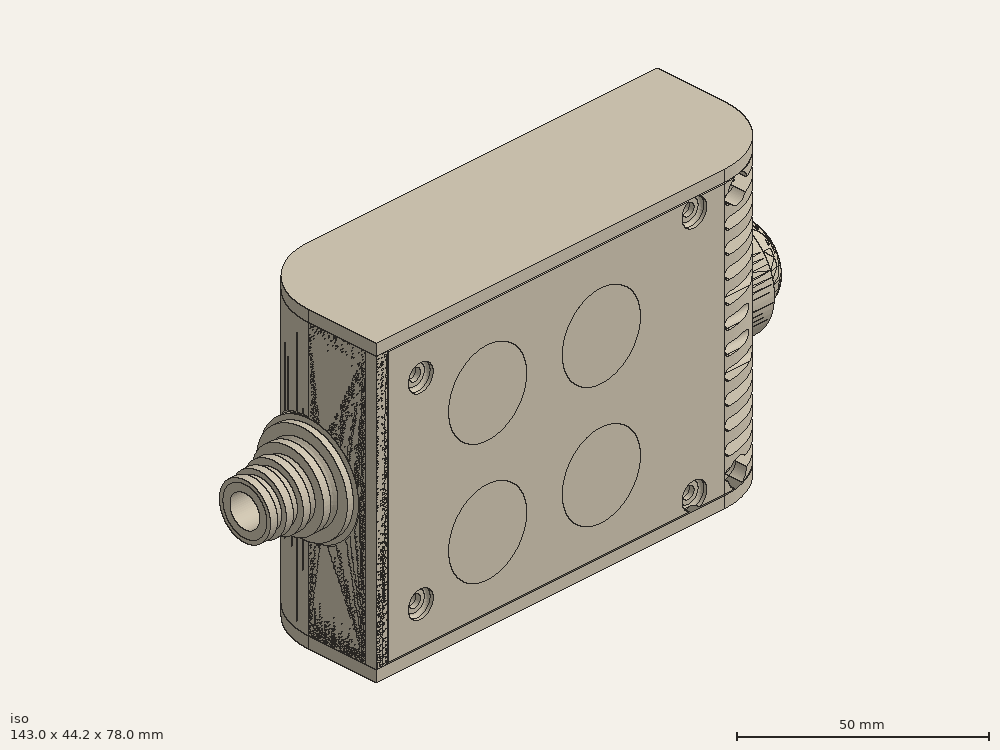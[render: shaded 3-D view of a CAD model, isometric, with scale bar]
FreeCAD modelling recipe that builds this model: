
FCSTD DOCUMENT  (FreeCAD 0.19R0.19.2)
Label: enclosure_123
License: All rights reserved
LicenseURL: http://en.wikipedia.org/wiki/All_rights_reserved
objects: Part::Feature×72, Part::Revolution×72, Part::MultiFuse×61, Sketcher::SketchObject×34, Part::Fillet×26, Part::Cut×24, Part::Extrusion×23, Part::Cylinder×22, Part::Box×12, App::MeasureDistance×4
note: 346 computed .brp shape members not serialized (recipe doc carries the construction recipe); baked Part::Feature solids carry a one-line shape summary decoded from their .brp

FEATURE [Sketcher::SketchObject] Sketch  label="topSketch"
  FullyConstrained = true
  sketch-geometry (13):
    g0: LineSegment StartX=117 StartY=19 StartZ=0 EndX=117 EndY=38 EndZ=0
    g1: ArcOfCircle CenterX=98 CenterY=19 CenterZ=0 NormalX=0 NormalY=0 NormalZ=1 AngleXU=0 Radius=19 StartAngle=5.7297 EndAngle=6.28319
    g2: LineSegment StartX=0 StartY=3 StartZ=0 EndX=0 EndY=19 EndZ=0
    g3: LineSegment StartX=19 StartY=38 StartZ=0 EndX=117 EndY=38 EndZ=0
    g4: ArcOfCircle CenterX=19 CenterY=19 CenterZ=0 NormalX=0 NormalY=0 NormalZ=1 AngleXU=0 Radius=19 StartAngle=1.5708 EndAngle=3.14159
    g5: ArcOfCircle CenterX=19 CenterY=19 CenterZ=0 NormalX=0 NormalY=0 NormalZ=1 AngleXU=0 Radius=16 StartAngle=1.5708 EndAngle=3.14159
    g6: ArcOfCircle CenterX=98 CenterY=19 CenterZ=0 NormalX=0 NormalY=0 NormalZ=1 AngleXU=0 Radius=16 StartAngle=5.60905 EndAngle=6.28319
    g7: LineSegment StartX=114 StartY=19 StartZ=0 EndX=114 EndY=35 EndZ=0
    g8: LineSegment StartX=110.5 StartY=9.01251 StartZ=0 EndX=114.163 EndY=9.01251 EndZ=0
    g9: LineSegment StartX=114 StartY=35 StartZ=0 EndX=19 EndY=35 EndZ=0
    g10: LineSegment StartX=0 StartY=3 StartZ=0 EndX=0 EndY=0 EndZ=0
    g11: LineSegment StartX=3 StartY=0 StartZ=0 EndX=0 EndY=0 EndZ=0
    g12: LineSegment StartX=3 StartY=19 StartZ=0 EndX=3 EndY=0 EndZ=0
  constraints (33):
    c: Vertical(g0)
    c: Distance(g0) = 19
    c: Block(g0)
    c: Coincident(g1,g0)
    c: Block(g1)
    c: Vertical(g2)
    c: Block(g2)
    c: Coincident(g3,g0)
    c: Horizontal(g3)
    c: Distance(g3) = 98
    c: Coincident(g4,g3)
    c: Coincident(g4,g2)
    c: Block(g4)
    c: Coincident(g5,g4)
    c: Coincident(g6,g1)
    c: Block(g6)
    c: Block(g5)
    c: Coincident(g7,g6)
    c: Vertical(g7)
    c: Coincident(g8,g6)
    c: Coincident(g8,g1)
    c: Coincident(g9,g7)
    c: Coincident(g9,g5)
    c: Horizontal(g9)
    c: Tangent(g9,g5)
    c: Coincident(g10,g2)
    c: Distance(g10) = 3
    c: Vertical(g10)
    c: Coincident(g11,g10)
    c: Horizontal(g11)
    c: Coincident(g12,g5)
    c: Coincident(g12,g11)
    c: Vertical(g12)
FEATURE [Sketcher::SketchObject] Sketch001  label="bottomSketch"
  FullyConstrained = true
  sketch-geometry (32):
    g0: LineSegment StartX=3.3 StartY=-6.03275e-07 StartZ=0 EndX=98 EndY=-6.03275e-07 EndZ=0
    g1: ArcOfCircle CenterX=98 CenterY=19 CenterZ=0 NormalX=0 NormalY=0 NormalZ=1 AngleXU=0 Radius=19 StartAngle=4.71239 EndAngle=5.71103
    g2: LineSegment StartX=6.3 StartY=8 StartZ=0 EndX=3.3 EndY=8 EndZ=0
    g3: LineSegment StartX=3.3 StartY=8 StartZ=0 EndX=3.3 EndY=-6.03275e-07 EndZ=0
    g4: ArcOfCircle CenterX=8.3 CenterY=5 CenterZ=0 NormalX=0 NormalY=0 NormalZ=1 AngleXU=0 Radius=2 StartAngle=3.14159 EndAngle=4.71239
    g5: LineSegment StartX=6.3 StartY=8 StartZ=0 EndX=6.3 EndY=5 EndZ=0
    g6: ArcOfCircle CenterX=98 CenterY=19 CenterZ=0 NormalX=0 NormalY=0 NormalZ=1 AngleXU=0 Radius=12.7 StartAngle=4.71239 EndAngle=6.28319
    g7: LineSegment StartX=94.7 StartY=3 StartZ=0 EndX=8.3 EndY=3 EndZ=0
    g8-g12: Circle x5 (B-spline internal-alignment scaffolding for g13; pole/knot coordinates omitted)
    g13: BSplineCurve PolesCount=5 KnotsCount=3 Degree=3 IsPeriodic=0
    g14: GeomPoint X=98 Y=6.3 Z=0
    g15: GeomPoint X=96.3938 Y=4.71946 Z=0
    g16: GeomPoint X=94.7 Y=3 Z=0
    g17-g23: Circle x7 (B-spline internal-alignment scaffolding for g24; pole/knot coordinates omitted)
    g24: BSplineCurve PolesCount=7 KnotsCount=5 Degree=3 IsPeriodic=0
    g25-g29: GeomPoint x5 (B-spline internal-alignment scaffolding for g24; pole/knot coordinates omitted)
    g30: ArcOfCircle CenterX=98 CenterY=19 CenterZ=0 NormalX=0 NormalY=0 NormalZ=1 AngleXU=0 Radius=15.7 StartAngle=5.81226 EndAngle=6.28319
    g31: LineSegment StartX=110.7 StartY=19 StartZ=0 EndX=113.7 EndY=19 EndZ=0
  constraints (41):
    c: Horizontal(g0)
    c: Coincident(g1,g0)
    c: Block(g1)
    c: Horizontal(g2)
    c: Distance(g2) = 3
    c: Coincident(g3,g2)
    c: Vertical(g3)
    c: Coincident(g3,g0)
    c: Block(g4)
    c: Block(g2)
    c: Coincident(g5,g2)
    c: Coincident(g5,g4)
    c: Vertical(g5)
    c: Coincident(g6,g1)
    c: Block(g6)
    c: Coincident(g7,g4)
    c: Horizontal(g7)
    c: Block(g0)
    c: Block(g7)
    c: Block(g3)
    c: Coincident(g13,g6)
    c: Weight(g8) = 1
    c: Equal(g8, g9-g12) x4
    c: Coincident(g13,g7)
    c: InternalAlignment(g8-g12 -> g13) x5
    c: InternalAlignment(g14,g13)
    c: InternalAlignment(g15,g13)
    c: InternalAlignment(g16,g13)
    c: Block(g13)
    c: Weight(g17) = 1
    c: Equal(g17, g18-g23) x6
    c: Coincident(g24,g1)
    c: InternalAlignment(g17-g23 -> g24) x7
    c: InternalAlignment(g25-g29 -> g24) x5
    c: Block(g24)
    c: Coincident(g30,g24)
    c: Coincident(g31,g6)
    c: Coincident(g31,g30)
    c: Horizontal(g31)
    c: Block(g31)
    c: Block(g30)
FEATURE [Part::Extrusion] Extrude  label="top"
  Base = -> Sketch
  Dir = (0,0,1)
  DirMode = 2
  FaceMakerClass = Part::FaceMakerBullseye
  LengthFwd = 72
  LengthRev = 0
  Solid = true
  Symmetric = false
FEATURE [Part::Extrusion] Extrude001  label="bottom"
  Base = -> Sketch001
  Dir = (0,0,1)
  DirMode = 2
  FaceMakerClass = Part::FaceMakerBullseye
  LengthFwd = 71.4
  LengthRev = 0
  Placement = pos=(0,0,0.3) rot=(0,0,1;0rad)
  Solid = true
  Symmetric = false
FEATURE [Sketcher::SketchObject] Sketch002  label="topSketch001"
  FullyConstrained = true
  sketch-geometry (6):
    g0: LineSegment StartX=19 StartY=38 StartZ=0 EndX=117 EndY=38 EndZ=0
    g1: ArcOfCircle CenterX=19 CenterY=19 CenterZ=0 NormalX=0 NormalY=0 NormalZ=1 AngleXU=0 Radius=19 StartAngle=1.5708 EndAngle=3.14159
    g2: LineSegment StartX=117 StartY=38 StartZ=0 EndX=117 EndY=19 EndZ=0
    g3: LineSegment StartX=98 StartY=1.0161e-12 StartZ=0 EndX=5.22862e-06 EndY=1.0161e-12 EndZ=0
    g4: LineSegment StartX=5.22862e-06 StartY=19 StartZ=0 EndX=5.22862e-06 EndY=1.0161e-12 EndZ=0
    g5: ArcOfCircle CenterX=98 CenterY=19 CenterZ=0 NormalX=0 NormalY=0 NormalZ=1 AngleXU=0 Radius=19 StartAngle=4.71239 EndAngle=6.28319
  constraints (16):
    c: Horizontal(g0)
    c: Distance(g0) = 98
    c: Coincident(g1,g0)
    c: Block(g1)
    c: Coincident(g2,g0)
    c: Vertical(g2)
    c: Distance(g2) = 19
    c: Horizontal(g3)
    c: Coincident(g4,g1)
    c: Vertical(g4)
    c: Coincident(g3,g4)
    c: Block(g3)
    c: Coincident(g5,g2)
    c: Coincident(g5,g3)
    c: Block(g0)
    c: Block(g5)
FEATURE [Part::Extrusion] Extrude002  label="sideA"
  Base = -> Sketch002
  Dir = (0,0,1)
  DirMode = 2
  FaceMakerClass = Part::FaceMakerBullseye
  LengthFwd = 3
  LengthRev = 0
  Placement = pos=(0,0,-3) rot=(0,0,1;0rad)
  Solid = true
  Symmetric = false
FEATURE [Sketcher::SketchObject] Sketch003  label="topSketch002"
  FullyConstrained = true
  sketch-geometry (6):
    g0: LineSegment StartX=19 StartY=38 StartZ=0 EndX=117 EndY=38 EndZ=0
    g1: ArcOfCircle CenterX=19 CenterY=19 CenterZ=0 NormalX=0 NormalY=0 NormalZ=1 AngleXU=0 Radius=19 StartAngle=1.5708 EndAngle=3.14159
    g2: LineSegment StartX=117 StartY=38 StartZ=0 EndX=117 EndY=19 EndZ=0
    g3: LineSegment StartX=98 StartY=1.0161e-12 StartZ=0 EndX=5.22862e-06 EndY=1.0161e-12 EndZ=0
    g4: LineSegment StartX=5.22862e-06 StartY=19 StartZ=0 EndX=5.22862e-06 EndY=1.0161e-12 EndZ=0
    g5: ArcOfCircle CenterX=98 CenterY=19 CenterZ=0 NormalX=0 NormalY=0 NormalZ=1 AngleXU=0 Radius=19 StartAngle=4.71239 EndAngle=6.28319
  constraints (16):
    c: Horizontal(g0)
    c: Distance(g0) = 98
    c: Coincident(g1,g0)
    c: Block(g1)
    c: Coincident(g2,g0)
    c: Vertical(g2)
    c: Distance(g2) = 19
    c: Horizontal(g3)
    c: Coincident(g4,g1)
    c: Vertical(g4)
    c: Coincident(g3,g4)
    c: Block(g3)
    c: Coincident(g5,g2)
    c: Coincident(g5,g3)
    c: Block(g0)
    c: Block(g5)
FEATURE [Part::Extrusion] Extrude003  label="sideB"
  Base = -> Sketch003
  Dir = (0,0,1)
  DirMode = 2
  FaceMakerClass = Part::FaceMakerBullseye
  LengthFwd = 3
  LengthRev = 0
  Placement = pos=(0,0,72) rot=(0,0,1;0rad)
  Solid = true
  Symmetric = false
FEATURE [Sketcher::SketchObject] Sketch004
  FullyConstrained = true
  MapMode = 3
  Placement = pos=(0,0,0) rot=(1,0,0;1.5708rad)
  Support = -> [Extrude]
  sketch-geometry (8):
    g0: Circle CenterX=80.351 CenterY=-67.6202 CenterZ=0 NormalX=0 NormalY=0 NormalZ=1 AngleXU=0 Radius=2
    g1: Circle CenterX=80.351 CenterY=-67.6202 CenterZ=0 NormalX=0 NormalY=0 NormalZ=1 AngleXU=0 Radius=3
    g2: Circle CenterX=80.351 CenterY=-4.92017 CenterZ=0 NormalX=0 NormalY=0 NormalZ=1 AngleXU=0 Radius=2
    g3: Circle CenterX=80.351 CenterY=-4.92017 CenterZ=0 NormalX=0 NormalY=0 NormalZ=1 AngleXU=0 Radius=3
    g4: Circle CenterX=23.851 CenterY=-4.92017 CenterZ=0 NormalX=0 NormalY=0 NormalZ=1 AngleXU=0 Radius=2
    g5: Circle CenterX=23.851 CenterY=-4.92017 CenterZ=0 NormalX=0 NormalY=0 NormalZ=1 AngleXU=0 Radius=3
    g6: Circle CenterX=23.851 CenterY=-67.6202 CenterZ=0 NormalX=0 NormalY=0 NormalZ=1 AngleXU=0 Radius=2
    g7: Circle CenterX=23.851 CenterY=-67.6202 CenterZ=0 NormalX=0 NormalY=0 NormalZ=1 AngleXU=0 Radius=3
  constraints (8):
    c: Block(g3)
    c: Block(g2)
    c: Block(g1)
    c: Block(g0)
    c: Block(g6)
    c: Block(g7)
    c: Block(g4)
    c: Block(g5)
FEATURE [Part::Extrusion] Extrude004
  Base = -> Sketch004
  Dir = (0,-1,2e-16)
  DirMode = 2
  FaceMakerClass = Part::FaceMakerBullseye
  LengthFwd = 6
  LengthRev = 0
  Placement = pos=(0,9,0) rot=(0,0,1;0rad)
  Solid = true
  Symmetric = false
FEATURE [Sketcher::SketchObject] Sketch005
  FullyConstrained = true
  MapMode = 3
  Placement = pos=(0,0,0) rot=(1,0,0;1.5708rad)
  Support = -> [Extrude]
  sketch-geometry (8):
    g0: Circle CenterX=80.351 CenterY=-67.6202 CenterZ=0 NormalX=0 NormalY=0 NormalZ=1 AngleXU=0 Radius=3
    g1: Circle CenterX=80.351 CenterY=-4.92017 CenterZ=0 NormalX=0 NormalY=0 NormalZ=1 AngleXU=0 Radius=3
    g2: Circle CenterX=23.851 CenterY=-4.92017 CenterZ=0 NormalX=0 NormalY=0 NormalZ=1 AngleXU=0 Radius=3
    g3: Circle CenterX=23.851 CenterY=-67.6202 CenterZ=0 NormalX=0 NormalY=0 NormalZ=1 AngleXU=0 Radius=3
    g4: Circle CenterX=23.851 CenterY=-67.6202 CenterZ=0 NormalX=0 NormalY=0 NormalZ=1 AngleXU=0 Radius=5
    g5: Circle CenterX=80.351 CenterY=-67.6202 CenterZ=0 NormalX=0 NormalY=0 NormalZ=1 AngleXU=0 Radius=5
    g6: Circle CenterX=23.851 CenterY=-4.92017 CenterZ=0 NormalX=0 NormalY=0 NormalZ=1 AngleXU=0 Radius=5
    g7: Circle CenterX=80.351 CenterY=-4.92017 CenterZ=0 NormalX=0 NormalY=0 NormalZ=1 AngleXU=0 Radius=5
  constraints (8):
    c: Block(g1)
    c: Block(g0)
    c: Block(g3)
    c: Block(g2)
    c: Block(g5)
    c: Block(g4)
    c: Block(g6)
    c: Block(g7)
FEATURE [Part::Extrusion] Extrude005
  Base = -> Sketch005
  Dir = (0,-1,2e-16)
  DirMode = 2
  FaceMakerClass = Part::FaceMakerBullseye
  LengthFwd = 2
  LengthRev = 0
  Solid = true
  Symmetric = false
FEATURE [Sketcher::SketchObject] Sketch006
  FullyConstrained = true
  MapMode = 3
  Placement = pos=(0,0,0) rot=(1,0,0;1.5708rad)
  sketch-geometry (8):
    g0: Circle CenterX=80.351 CenterY=-67.6202 CenterZ=0 NormalX=0 NormalY=0 NormalZ=1 AngleXU=0 Radius=3
    g1: Circle CenterX=80.351 CenterY=-4.92017 CenterZ=0 NormalX=0 NormalY=0 NormalZ=1 AngleXU=0 Radius=3
    g2: Circle CenterX=23.851 CenterY=-4.92017 CenterZ=0 NormalX=0 NormalY=0 NormalZ=1 AngleXU=0 Radius=3
    g3: Circle CenterX=23.851 CenterY=-67.6202 CenterZ=0 NormalX=0 NormalY=0 NormalZ=1 AngleXU=0 Radius=3
    g4: Circle CenterX=23.851 CenterY=-67.6202 CenterZ=0 NormalX=0 NormalY=0 NormalZ=1 AngleXU=0 Radius=5
    g5: Circle CenterX=80.351 CenterY=-67.6202 CenterZ=0 NormalX=0 NormalY=0 NormalZ=1 AngleXU=0 Radius=5
    g6: Circle CenterX=23.851 CenterY=-4.92017 CenterZ=0 NormalX=0 NormalY=0 NormalZ=1 AngleXU=0 Radius=5
    g7: Circle CenterX=80.351 CenterY=-4.92017 CenterZ=0 NormalX=0 NormalY=0 NormalZ=1 AngleXU=0 Radius=5
  constraints (8):
    c: Block(g1)
    c: Block(g0)
    c: Block(g3)
    c: Block(g2)
    c: Block(g5)
    c: Block(g4)
    c: Block(g6)
    c: Block(g7)
FEATURE [Part::Extrusion] Extrude007
  Base = -> Sketch006
  Dir = (0,-1,2e-16)
  DirMode = 2
  FaceMakerClass = Part::FaceMakerBullseye
  LengthFwd = 2
  LengthRev = 0
  Solid = true
  Symmetric = false
FEATURE [Part::Fillet] Fillet
  Base = -> Extrude007
  Edges = 4 edges r=1.99: [Edge6,Edge12,Edge18,Edge24]
FEATURE [Part::Cut] Cut
  Base = -> Extrude005
  Placement = pos=(0,5,0) rot=(0,0,1;0rad)
  Tool = -> Fillet
FEATURE [Part::MultiFuse] Fusion  label="pCBScrews"
  Placement = pos=(-2.5,0,72.3) rot=(0,0,1;0rad)
  Shapes = -> [Extrude004,Cut]
FEATURE [App::MeasureDistance] Distance  label="Distance: 0.69 mm"
  Distance = 0.685967
  P1 = (24.0138,2.9647,0.3)
  P2 = (23.8901,3,-0.373787)
FEATURE [App::MeasureDistance] Distance001  label="Distance: 0.53 mm"
  Distance = 0.533607
  P1 = (80.2939,3,72.2334)
  P2 = (80.281,2.99661,71.7)
FEATURE [Part::Fillet] Fillet001
  Base = -> Extrude001
  Edges = 1 edges r=2.4: [Edge17]
FEATURE [Part::Fillet] Fillet002  label="bottom001"
  Base = -> Fillet001
  Edges = 1 edges r=2.4: [Edge36]
FEATURE [Part::Fillet] Fillet003  label="top001"
  Base = -> Extrude
  Edges = 1 edges r=2: [Edge1]
FEATURE [Sketcher::SketchObject] Sketch007
  FullyConstrained = true
  sketch-geometry (16):
    g0: LineSegment StartX=4 StartY=0 StartZ=0 EndX=4 EndY=2.4 EndZ=0
    g1: LineSegment StartX=4 StartY=2.4 StartZ=0 EndX=7 EndY=2.4 EndZ=0
    g2: LineSegment StartX=4 StartY=0 StartZ=0 EndX=5.7 EndY=0 EndZ=0
    g3: LineSegment StartX=5.7 StartY=0 StartZ=0 EndX=5.7 EndY=-5.6 EndZ=0
    g4-g8: Circle x5 (B-spline internal-alignment scaffolding for g9; pole/knot coordinates omitted)
    g9: BSplineCurve PolesCount=5 KnotsCount=3 Degree=3 IsPeriodic=0
    g10: GeomPoint X=7 Y=2.4 Z=0
    g11: GeomPoint X=10.4582 Y=-1.55472 Z=0
    g12: GeomPoint X=14 Y=-5.6 Z=0
    g13: LineSegment StartX=14 StartY=-5.6 StartZ=0 EndX=14 EndY=-14.1 EndZ=0
    g14: LineSegment StartX=14 StartY=-14.1 StartZ=0 EndX=6.5 EndY=-14.1 EndZ=0
    g15: LineSegment StartX=5.7 StartY=-5.6 StartZ=0 EndX=6.5 EndY=-14.1 EndZ=0
  constraints (28):
    c: Distance(g0) = 2.4
    c: Vertical(g0)
    c: Block(g0)
    c: Coincident(g1,g0)
    c: Horizontal(g1)
    c: Distance(g1) = 3
    c: Coincident(g2,g0)
    c: Horizontal(g2)
    c: Distance(g2) = 1.7
    c: Coincident(g3,g2)
    c: Vertical(g3)
    c: Distance(g3) = 5.6
    c: Coincident(g9,g1)
    c: Weight(g4) = 1
    c: Equal(g4, g5-g8) x4
    c: InternalAlignment(g4-g8 -> g9) x5
    c: InternalAlignment(g10,g9)
    c: InternalAlignment(g11,g9)
    c: InternalAlignment(g12,g9)
    c: Block(g9)
    c: Coincident(g13,g9)
    c: Vertical(g13)
    c: Distance(g13) = 8.5
    c: Coincident(g14,g13)
    c: Horizontal(g14)
    c: Distance(g14) = 7.5
    c: Coincident(g15,g3)
    c: Coincident(g15,g14)
FEATURE [Part::Feature] Face
  shape: bbox 10 x 16.5 x 2e-07 mm, 1 faces, 0 solids (baked)
FEATURE [Part::Revolution] Revolve  label="plugHousing"
  Angle = 360
  Axis = (0,1,0)
  Base = (0,0,0)
  FaceMakerClass = Part::FaceMakerBullseye
  Placement = pos=(0,0,36.15) rot=(0,0,1;0rad)
  Solid = false
  Source = -> Face
  Symmetric = false
FEATURE [Part::Feature] Face001
  shape: bbox 10 x 16.5 x 2e-07 mm, 1 faces, 0 solids (baked)
FEATURE [Part::Revolution] Revolve001  label="plugHousing001"
  Angle = 360
  Axis = (0,1,0)
  Base = (0,0,0)
  FaceMakerClass = Part::FaceMakerBullseye
  Placement = pos=(0,0,36.15) rot=(0,0,1;0rad)
  Solid = false
  Source = -> Face001
  Symmetric = false
FEATURE [Part::MultiFuse] Fusion001  label="plugHousing002"
  Placement = pos=(0,0,0) rot=(0,0,1;1.5708rad)
  Shapes = -> [Revolve001,Revolve]
FEATURE [Part::Feature] Face002
  shape: bbox 10 x 16.5 x 2e-07 mm, 1 faces, 0 solids (baked)
FEATURE [Part::Revolution] Revolve003  label="plugHousing005"
  Angle = 360
  Axis = (0,1,0)
  Base = (0,0,0)
  FaceMakerClass = Part::FaceMakerBullseye
  Placement = pos=(0,0,36.15) rot=(0,0,1;0rad)
  Solid = false
  Source = -> Face002
  Symmetric = false
FEATURE [Part::Feature] Face003
  shape: bbox 10 x 16.5 x 2e-07 mm, 1 faces, 0 solids (baked)
FEATURE [Part::Revolution] Revolve002  label="plugHousing003"
  Angle = 360
  Axis = (0,1,0)
  Base = (0,0,0)
  FaceMakerClass = Part::FaceMakerBullseye
  Placement = pos=(0,0,36.15) rot=(0,0,1;0rad)
  Solid = false
  Source = -> Face003
  Symmetric = false
FEATURE [Part::MultiFuse] Fusion002  label="plugHousing004"
  Placement = pos=(0,0,0) rot=(0,0,1;1.5708rad)
  Shapes = -> [Revolve002,Revolve003]
FEATURE [Part::MultiFuse] Fusion003  label="plugHousing006"
  Placement = pos=(0,19,0) rot=(0,0,1;3.14159rad)
  Shapes = -> [Fusion002,Fusion001]
FEATURE [Part::Feature] Face004
  shape: bbox 10 x 16.5 x 2e-07 mm, 1 faces, 0 solids (baked)
FEATURE [Part::Revolution] Revolve006  label="plugHousing010"
  Angle = 360
  Axis = (0,1,0)
  Base = (0,0,0)
  FaceMakerClass = Part::FaceMakerBullseye
  Placement = pos=(0,0,36.15) rot=(0,0,1;0rad)
  Solid = false
  Source = -> Face004
  Symmetric = false
FEATURE [Part::Feature] Face005
  shape: bbox 10 x 16.5 x 2e-07 mm, 1 faces, 0 solids (baked)
FEATURE [Part::Revolution] Revolve007  label="plugHousing011"
  Angle = 360
  Axis = (0,1,0)
  Base = (0,0,0)
  FaceMakerClass = Part::FaceMakerBullseye
  Placement = pos=(0,0,36.15) rot=(0,0,1;0rad)
  Solid = false
  Source = -> Face005
  Symmetric = false
FEATURE [Part::Feature] Face006
  shape: bbox 10 x 16.5 x 2e-07 mm, 1 faces, 0 solids (baked)
FEATURE [Part::Revolution] Revolve004  label="plugHousing007"
  Angle = 360
  Axis = (0,1,0)
  Base = (0,0,0)
  FaceMakerClass = Part::FaceMakerBullseye
  Placement = pos=(0,0,36.15) rot=(0,0,1;0rad)
  Solid = false
  Source = -> Face006
  Symmetric = false
FEATURE [Part::MultiFuse] Fusion004  label="plugHousing009"
  Placement = pos=(0,0,0) rot=(0,0,1;1.5708rad)
  Shapes = -> [Revolve004,Revolve007]
FEATURE [Part::Feature] Face007
  shape: bbox 10 x 16.5 x 2e-07 mm, 1 faces, 0 solids (baked)
FEATURE [Part::Revolution] Revolve005  label="plugHousing008"
  Angle = 360
  Axis = (0,1,0)
  Base = (0,0,0)
  FaceMakerClass = Part::FaceMakerBullseye
  Placement = pos=(0,0,36.15) rot=(0,0,1;0rad)
  Solid = false
  Source = -> Face007
  Symmetric = false
FEATURE [Part::MultiFuse] Fusion005  label="plugHousing012"
  Placement = pos=(0,0,0) rot=(0,0,1;1.5708rad)
  Shapes = -> [Revolve006,Revolve005]
FEATURE [Part::MultiFuse] Fusion006  label="plugHousing013"
  Placement = pos=(0,19,0) rot=(0,0,1;3.14159rad)
  Shapes = -> [Fusion005,Fusion004]
FEATURE [Part::MultiFuse] Fusion007  label="plugHousing014"
  Placement = pos=(122.621,0,-0.15) rot=(0,0,1;0rad)
  Shapes = -> [Fusion003,Fusion006]
FEATURE [Part::Cylinder] Cylinder002
  Angle = 360
  AttacherType = Attacher::AttachEngine3D
  Height = 20
  Placement = pos=(0,0,36.15) rot=(0,0,1;0rad)
  Radius = 4
FEATURE [Part::Cylinder] Cylinder003
  Angle = 360
  AttacherType = Attacher::AttachEngine3D
  Height = 10
  Placement = pos=(0,0,36.15) rot=(0,0,1;0rad)
  Radius = 4
FEATURE [Part::MultiFuse] Fusion009  label="removeToCreateHoleForPlugHousing"
  Placement = pos=(70,19,36.15) rot=(0,1,0;1.5708rad)
  Shapes = -> [Cylinder002,Cylinder003]
FEATURE [Part::Cylinder] Cylinder004
  Angle = 360
  AttacherType = Attacher::AttachEngine3D
  Height = 20
  Placement = pos=(0,0,36.15) rot=(0,0,1;0rad)
  Radius = 4
FEATURE [Part::Cylinder] Cylinder005
  Angle = 360
  AttacherType = Attacher::AttachEngine3D
  Height = 10
  Placement = pos=(0,0,36.15) rot=(0,0,1;0rad)
  Radius = 4
FEATURE [Part::MultiFuse] Fusion010  label="removeToCreateHoleForPlugHousing001"
  Placement = pos=(70,19,36.15) rot=(0,1,0;1.5708rad)
  Shapes = -> [Cylinder004,Cylinder005]
FEATURE [Part::Cut] Cut001
  Base = -> Fillet003
  Tool = -> Fusion010
FEATURE [Part::Cut] Cut002  label="Bottom"
  Base = -> Fillet002
  Tool = -> Fusion009
FEATURE [Part::Feature] Face008
  shape: bbox 10 x 16.5 x 2e-07 mm, 1 faces, 0 solids (baked)
FEATURE [Part::Revolution] Revolve011  label="plugHousing021"
  Angle = 360
  Axis = (0,1,0)
  Base = (0,0,0)
  FaceMakerClass = Part::FaceMakerBullseye
  Placement = pos=(0,0,36.15) rot=(0,0,1;0rad)
  Solid = false
  Source = -> Face008
  Symmetric = false
FEATURE [Part::Feature] Face009
  shape: bbox 10 x 16.5 x 2e-07 mm, 1 faces, 0 solids (baked)
FEATURE [Part::Revolution] Revolve012  label="plugHousing022"
  Angle = 360
  Axis = (0,1,0)
  Base = (0,0,0)
  FaceMakerClass = Part::FaceMakerBullseye
  Placement = pos=(0,0,36.15) rot=(0,0,1;0rad)
  Solid = false
  Source = -> Face009
  Symmetric = false
FEATURE [Part::Feature] Face010 .. Face013  x4 (patterned run collapsed; names and placements below)
  shape: bbox 10 x 16.5 x 2e-07 mm, 1 faces, 0 solids (baked)
FEATURE [Part::Revolution] Revolve015  label="plugHousing027"
  Angle = 360
  Axis = (0,1,0)
  Base = (0,0,0)
  FaceMakerClass = Part::FaceMakerBullseye
  Placement = pos=(0,0,36.15) rot=(0,0,1;0rad)
  Solid = false
  Source = -> Face013
  Symmetric = false
FEATURE [Part::Feature] Face014
  shape: bbox 10 x 16.5 x 2e-07 mm, 1 faces, 0 solids (baked)
FEATURE [Part::Feature] Face015
  shape: bbox 10 x 16.5 x 2e-07 mm, 1 faces, 0 solids (baked)
FEATURE [Part::Feature] Face016
  shape: bbox 10 x 16.5 x 2e-07 mm, 1 faces, 0 solids (baked)
FEATURE [Part::Revolution] Revolve019  label="plugHousing033"
  Angle = 360
  Axis = (0,1,0)
  Base = (0,0,0)
  FaceMakerClass = Part::FaceMakerBullseye
  Placement = pos=(0,0,36.15) rot=(0,0,1;0rad)
  Solid = false
  Source = -> Face016
  Symmetric = false
FEATURE [Part::Feature] Face017
  shape: bbox 10 x 16.5 x 2e-07 mm, 1 faces, 0 solids (baked)
FEATURE [Part::Revolution] Revolve020  label="plugHousing034"
  Angle = 360
  Axis = (0,1,0)
  Base = (0,0,0)
  FaceMakerClass = Part::FaceMakerBullseye
  Placement = pos=(0,0,36.15) rot=(0,0,1;0rad)
  Solid = false
  Source = -> Face017
  Symmetric = false
FEATURE [Part::Feature] Face018
  shape: bbox 10 x 16.5 x 2e-07 mm, 1 faces, 0 solids (baked)
FEATURE [Part::Revolution] Revolve016  label="plugHousing030"
  Angle = 360
  Axis = (0,1,0)
  Base = (0,0,0)
  FaceMakerClass = Part::FaceMakerBullseye
  Placement = pos=(0,0,36.15) rot=(0,0,1;0rad)
  Solid = false
  Source = -> Face018
  Symmetric = false
FEATURE [Part::MultiFuse] Fusion020  label="plugHousing038"
  Placement = pos=(0,0,0) rot=(0,0,1;1.5708rad)
  Shapes = -> [Revolve016,Revolve020]
FEATURE [Part::Feature] Face019
  shape: bbox 10 x 16.5 x 2e-07 mm, 1 faces, 0 solids (baked)
FEATURE [Part::Feature] Face020
  shape: bbox 10 x 16.5 x 2e-07 mm, 1 faces, 0 solids (baked)
FEATURE [Part::Revolution] Revolve017  label="plugHousing031"
  Angle = 360
  Axis = (0,1,0)
  Base = (0,0,0)
  FaceMakerClass = Part::FaceMakerBullseye
  Placement = pos=(0,0,36.15) rot=(0,0,1;0rad)
  Solid = false
  Source = -> Face020
  Symmetric = false
FEATURE [Part::MultiFuse] Fusion021  label="plugHousing039"
  Placement = pos=(0,0,0) rot=(0,0,1;1.5708rad)
  Shapes = -> [Revolve019,Revolve017]
FEATURE [Part::MultiFuse] Fusion023  label="plugHousing041"
  Placement = pos=(0,19,0) rot=(0,0,1;3.14159rad)
  Shapes = -> [Fusion021,Fusion020]
FEATURE [Part::Revolution] Revolve022  label="plugHousing043"
  Angle = 360
  Axis = (0,1,0)
  Base = (0,0,0)
  FaceMakerClass = Part::FaceMakerBullseye
  Placement = pos=(0,0,36.15) rot=(0,0,1;0rad)
  Solid = false
  Source = -> Face019
  Symmetric = false
FEATURE [Part::Feature] Face021
  shape: bbox 10 x 16.5 x 2e-07 mm, 1 faces, 0 solids (baked)
FEATURE [Part::Revolution] Revolve023  label="plugHousing044"
  Angle = 360
  Axis = (0,1,0)
  Base = (0,0,0)
  FaceMakerClass = Part::FaceMakerBullseye
  Placement = pos=(0,0,36.15) rot=(0,0,1;0rad)
  Solid = false
  Source = -> Face021
  Symmetric = false
FEATURE [Part::Feature] Face022
  shape: bbox 10 x 16.5 x 2e-07 mm, 1 faces, 0 solids (baked)
FEATURE [Part::Revolution] Revolve018  label="plugHousing032"
  Angle = 360
  Axis = (0,1,0)
  Base = (0,0,0)
  FaceMakerClass = Part::FaceMakerBullseye
  Placement = pos=(0,0,36.15) rot=(0,0,1;0rad)
  Solid = false
  Source = -> Face022
  Symmetric = false
FEATURE [Part::MultiFuse] Fusion022  label="plugHousing040"
  Placement = pos=(0,0,0) rot=(0,0,1;1.5708rad)
  Shapes = -> [Revolve018,Revolve023]
FEATURE [Part::Feature] Face023
  shape: bbox 10 x 16.5 x 2e-07 mm, 1 faces, 0 solids (baked)
FEATURE [Part::Revolution] Revolve021  label="plugHousing035"
  Angle = 360
  Axis = (0,1,0)
  Base = (0,0,0)
  FaceMakerClass = Part::FaceMakerBullseye
  Placement = pos=(0,0,36.15) rot=(0,0,1;0rad)
  Solid = false
  Source = -> Face023
  Symmetric = false
FEATURE [Part::MultiFuse] Fusion018  label="plugHousing036"
  Placement = pos=(0,0,0) rot=(0,0,1;1.5708rad)
  Shapes = -> [Revolve022,Revolve021]
FEATURE [Part::MultiFuse] Fusion019  label="plugHousing037"
  Placement = pos=(0,19,0) rot=(0,0,1;3.14159rad)
  Shapes = -> [Fusion018,Fusion022]
FEATURE [Part::MultiFuse] Fusion024  label="plugHousing042"
  Placement = pos=(122.621,0,-0.15) rot=(0,0,1;0rad)
  Shapes = -> [Fusion023,Fusion019]
FEATURE [Part::Cylinder] Cylinder006
  Angle = 360
  AttacherType = Attacher::AttachEngine3D
  Height = 20
  Placement = pos=(0,0,36.15) rot=(0,0,1;0rad)
  Radius = 14.3
FEATURE [Part::Cylinder] Cylinder007
  Angle = 360
  AttacherType = Attacher::AttachEngine3D
  Height = 10
  Placement = pos=(0,0,36.15) rot=(0,0,1;0rad)
  Radius = 4
FEATURE [Part::MultiFuse] Fusion026  label="removeToCreteHoleForPlugHousing"
  Placement = pos=(70,19,36) rot=(0,1,0;1.5708rad)
  Shapes = -> [Cylinder006,Cylinder007]
FEATURE [Part::Box] Box001  label="Cube001"
  AttacherType = Attacher::AttachEngine3D
  Height = 28
  Length = 3
  Placement = pos=(110.7,19,22) rot=(0,0,1;0rad)
  Width = 15.7
FEATURE [Part::Cut] Cut003  label="top002"
  Base = -> Cut001
  Tool = -> Fusion007
FEATURE [Part::Revolution] Revolve008  label="plugHousing015"
  Angle = 360
  Axis = (0,1,0)
  Base = (0,0,0)
  FaceMakerClass = Part::FaceMakerBullseye
  Placement = pos=(0,0,36.15) rot=(0,0,1;0rad)
  Solid = false
  Source = -> Face010
  Symmetric = false
FEATURE [Part::MultiFuse] Fusion013  label="plugHousing020"
  Placement = pos=(0,0,0) rot=(0,0,1;1.5708rad)
  Shapes = -> [Revolve008,Revolve012]
FEATURE [Part::Cut] Cut004  label="top003"
  Base = -> Cut003
  Placement = pos=(1,0,0) rot=(0,0,1;0rad)
  Tool = -> Fusion026
FEATURE [Part::Cylinder] Cylinder008
  Angle = 360
  AttacherType = Attacher::AttachEngine3D
  Height = 20
  Placement = pos=(0,0,36.15) rot=(0,0,1;0rad)
  Radius = 10.3
FEATURE [Part::Cylinder] Cylinder009
  Angle = 360
  AttacherType = Attacher::AttachEngine3D
  Height = 10
  Placement = pos=(0,0,36.15) rot=(0,0,1;0rad)
  Radius = 4
FEATURE [Part::MultiFuse] Fusion027  label="removeToCreteHoleForPlugHousing001"
  Placement = pos=(70,19,36) rot=(0,1,0;1.5708rad)
  Shapes = -> [Cylinder008,Cylinder009]
FEATURE [Part::Cut] Cut005  label="plugHousingTab"
  Base = -> Box001
  Tool = -> Fusion027
FEATURE [Part::MultiFuse] Fusion028  label="plugHousing045"
  Shapes = -> [Fusion024,Cut005]
FEATURE [Part::Box] Box002  label="Cube002"
  AttacherType = Attacher::AttachEngine3D
  Height = 28.8
  Length = 3
  Placement = pos=(107.3,28,21.6) rot=(0,0,1;0rad)
  Width = 7
FEATURE [Part::Box] Box003  label="Cube003"
  AttacherType = Attacher::AttachEngine3D
  Height = 3
  Length = 6.4
  Placement = pos=(107.3,28,18.6) rot=(0,0,1;0rad)
  Width = 7
FEATURE [Part::Box] Box004  label="Cube004"
  AttacherType = Attacher::AttachEngine3D
  Height = 3
  Length = 6.4
  Placement = pos=(107.3,28,50.4) rot=(0,0,1;0rad)
  Width = 7
FEATURE [Part::MultiFuse] Fusion029  label="plugHousingBracketHolder"
  Shapes = -> [Box004,Box002,Box003]
FEATURE [Part::Cylinder] Cylinder010
  Angle = 360
  AttacherType = Attacher::AttachEngine3D
  Height = 20
  Placement = pos=(0,0,36.15) rot=(0,0,1;0rad)
  Radius = 14.3
FEATURE [Part::Cylinder] Cylinder011
  Angle = 360
  AttacherType = Attacher::AttachEngine3D
  Height = 10
  Placement = pos=(0,0,36.15) rot=(0,0,1;0rad)
  Radius = 4
FEATURE [Part::MultiFuse] Fusion030  label="removeToCreteHoleForPlugHousing002"
  Placement = pos=(70,19,36) rot=(0,1,0;1.5708rad)
  Shapes = -> [Cylinder010,Cylinder011]
FEATURE [Part::Cut] Cut006  label="plugHousingBracketHolder001"
  Base = -> Fusion029
  Tool = -> Fusion030
FEATURE [Part::Cylinder] Cylinder012
  Angle = 360
  AttacherType = Attacher::AttachEngine3D
  Height = 20
  Placement = pos=(0,0,36.15) rot=(0,0,1;0rad)
  Radius = 7
FEATURE [Part::Cylinder] Cylinder013
  Angle = 360
  AttacherType = Attacher::AttachEngine3D
  Height = 10
  Placement = pos=(0,0,36.15) rot=(0,0,1;0rad)
  Radius = 4
FEATURE [Part::MultiFuse] Fusion032  label="removeToCreteHoleForPlugHousing003"
  Placement = pos=(70,19,36) rot=(0,1,0;1.5708rad)
  Shapes = -> [Cylinder012,Cylinder013]
FEATURE [Part::Cut] Cut007  label="bottom002"
  Base = -> Cut002
  Tool = -> Fusion032
FEATURE [Sketcher::SketchObject] Sketch008
  FullyConstrained = true
  sketch-geometry (54):
    g0: LineSegment StartX=-4.2 StartY=0 StartZ=0 EndX=-6.2 EndY=0 EndZ=0
    g1: LineSegment StartX=-14 StartY=-18 StartZ=0 EndX=-14 EndY=-26.5 EndZ=0
    g2: LineSegment StartX=-4.2 StartY=0 StartZ=0 EndX=-4.2 EndY=-13.4877 EndZ=0
    g3: Circle CenterX=-4.2 CenterY=-13.4877 CenterZ=0 NormalX=0 NormalY=0 NormalZ=1 AngleXU=0 Radius=1
    g4: Circle CenterX=-4.2 CenterY=-26.5 CenterZ=0 NormalX=0 NormalY=0 NormalZ=1 AngleXU=0 Radius=1
    g5: Circle CenterX=-8.2 CenterY=-26.5 CenterZ=0 NormalX=0 NormalY=0 NormalZ=1 AngleXU=0 Radius=1
    g6: BSplineCurve PolesCount=3 KnotsCount=2 Degree=2 IsPeriodic=0
    g7: GeomPoint X=-4.2 Y=-13.4877 Z=0
    g8: GeomPoint X=-8.2 Y=-26.5 Z=0
    g9: LineSegment StartX=-14 StartY=-26.5 StartZ=0 EndX=-8.2 EndY=-26.5 EndZ=0
    g10: LineSegment StartX=-10.15 StartY=-12 StartZ=0 EndX=-10.15 EndY=-14 EndZ=0
    g11: LineSegment StartX=-12.8401 StartY=-16 StartZ=0 EndX=-10.1571 EndY=-16 EndZ=0
    g12: LineSegment StartX=-10.15 StartY=-14 StartZ=0 EndX=-8.70761 EndY=-14 EndZ=0
    g13: LineSegment StartX=-12.8401 StartY=-16 StartZ=0 EndX=-12.8401 EndY=-17.6958 EndZ=0
    g14: LineSegment StartX=-10.15 StartY=-12 StartZ=0 EndX=-7.79258 EndY=-12 EndZ=0
    g15: Circle CenterX=-6.2215 CenterY=-2 CenterZ=0 NormalX=0 NormalY=0 NormalZ=1 AngleXU=0 Radius=1
    g16: Circle CenterX=-6.22762 CenterY=-2.58724 CenterZ=0 NormalX=0 NormalY=0 NormalZ=1 AngleXU=0 Radius=1
    g17: Circle CenterX=-6.32538 CenterY=-4 CenterZ=0 NormalX=0 NormalY=0 NormalZ=1 AngleXU=0 Radius=1
    g18: BSplineCurve PolesCount=3 KnotsCount=2 Degree=2 IsPeriodic=0
    g19: GeomPoint X=-6.2215 Y=-2 Z=0
    g20: GeomPoint X=-6.32538 Y=-4 Z=0
    g21: Circle CenterX=-6.48644 CenterY=-5.99526 CenterZ=0 NormalX=0 NormalY=0 NormalZ=1 AngleXU=0 Radius=1
    g22: Circle CenterX=-6.58486 CenterY=-6.99526 CenterZ=0 NormalX=0 NormalY=0 NormalZ=1 AngleXU=0 Radius=1
    g23: Circle CenterX=-6.77343 CenterY=-8 CenterZ=0 NormalX=0 NormalY=0 NormalZ=1 AngleXU=0 Radius=1
    g24: BSplineCurve PolesCount=3 KnotsCount=2 Degree=2 IsPeriodic=0
    g25: GeomPoint X=-6.48644 Y=-5.99526 Z=0
    g26: GeomPoint X=-6.77343 Y=-8 Z=0
    g27: Circle CenterX=-7.19003 CenterY=-10 CenterZ=0 NormalX=0 NormalY=0 NormalZ=1 AngleXU=0 Radius=1
    g28: Circle CenterX=-7.44407 CenterY=-11.0915 CenterZ=0 NormalX=0 NormalY=0 NormalZ=1 AngleXU=0 Radius=1
    g29: Circle CenterX=-7.79258 CenterY=-12 CenterZ=0 NormalX=0 NormalY=0 NormalZ=1 AngleXU=0 Radius=1
    g30: BSplineCurve PolesCount=3 KnotsCount=2 Degree=2 IsPeriodic=0
    g31: GeomPoint X=-7.19003 Y=-10 Z=0
    g32: GeomPoint X=-7.79258 Y=-12 Z=0
    g33: Circle CenterX=-8.70761 CenterY=-14 CenterZ=0 NormalX=0 NormalY=0 NormalZ=1 AngleXU=0 Radius=1
    g34: Circle CenterX=-9.33087 CenterY=-15.1837 CenterZ=0 NormalX=0 NormalY=0 NormalZ=1 AngleXU=0 Radius=1
    g35: Circle CenterX=-10.1571 CenterY=-16 CenterZ=0 NormalX=0 NormalY=0 NormalZ=1 AngleXU=0 Radius=1
    g36: BSplineCurve PolesCount=3 KnotsCount=2 Degree=2 IsPeriodic=0
    g37: GeomPoint X=-8.70761 Y=-14 Z=0
    g38: GeomPoint X=-10.1571 Y=-16 Z=0
    g39: Circle CenterX=-12.8401 CenterY=-17.6958 CenterZ=0 NormalX=0 NormalY=0 NormalZ=1 AngleXU=0 Radius=1
    g40: Circle CenterX=-13.3521 CenterY=-17.9027 CenterZ=0 NormalX=0 NormalY=0 NormalZ=1 AngleXU=0 Radius=1
    g41: Circle CenterX=-14 CenterY=-18 CenterZ=0 NormalX=0 NormalY=0 NormalZ=1 AngleXU=0 Radius=1
    g42: BSplineCurve PolesCount=3 KnotsCount=2 Degree=2 IsPeriodic=0
    g43: GeomPoint X=-12.8401 Y=-17.6958 Z=0
    g44: GeomPoint X=-14 Y=-18 Z=0
    g45: LineSegment StartX=-6.2 StartY=0 StartZ=0 EndX=-7.2 EndY=0 EndZ=0
    g46: LineSegment StartX=-7.2 StartY=0 StartZ=0 EndX=-7.2 EndY=-2 EndZ=0
    g47: LineSegment StartX=-7.2 StartY=-2 StartZ=0 EndX=-6.2215 EndY=-2 EndZ=0
    g48: LineSegment StartX=-6.32538 StartY=-4 StartZ=0 EndX=-7.65538 EndY=-4 EndZ=0
    g49: LineSegment StartX=-7.65538 StartY=-4 StartZ=0 EndX=-7.65538 EndY=-5.99526 EndZ=0
    g50: LineSegment StartX=-7.65538 StartY=-5.99526 StartZ=0 EndX=-6.48644 EndY=-5.99526 EndZ=0
    g51: LineSegment StartX=-6.77343 StartY=-8 StartZ=0 EndX=-8.43343 EndY=-8 EndZ=0
    g52: LineSegment StartX=-8.43343 StartY=-8 StartZ=0 EndX=-8.43343 EndY=-10 EndZ=0
    g53: LineSegment StartX=-8.43343 StartY=-10 StartZ=0 EndX=-7.19003 EndY=-10 EndZ=0
  constraints (112):
    c: Horizontal(g0)
    c: Distance(g0) = 2
    c: Block(g0)
    c: Vertical(g1)
    c: Coincident(g2,g0)
    c: Vertical(g2)
    c: Block(g2)
    c: Coincident(g6,g2)
    c: Weight(g3) = 1
    c: Equal(g3,g4)
    c: Equal(g3,g5)
    c: InternalAlignment(g3,g6)
    c: InternalAlignment(g4,g6)
    c: InternalAlignment(g5,g6)
    c: InternalAlignment(g7,g6)
    c: InternalAlignment(g8,g6)
    c: Block(g6)
    c: Coincident(g9,g1)
    c: Coincident(g9,g6)
    c: Horizontal(g9)
    c: Vertical(g10)
    c: Block(g10)
    c: Horizontal(g11)
    c: Block(g11)
    c: Coincident(g12,g10)
    c: Horizontal(g12)
    c: Block(g12)
    c: Coincident(g13,g11)
    c: Vertical(g13)
    c: Block(g13)
    c: Coincident(g14,g10)
    c: Horizontal(g14)
    c: Block(g14)
    c: Block(g9)
    c: Block(g1)
    c: Weight(g15) = 1
    c: Equal(g15,g16)
    c: Equal(g15,g17)
    c: InternalAlignment(g15,g18)
    c: InternalAlignment(g16,g18)
    c: InternalAlignment(g17,g18)
    c: InternalAlignment(g19,g18)
    c: InternalAlignment(g20,g18)
    c: Weight(g21) = 1
    c: Equal(g21,g22)
    c: Equal(g21,g23)
    c: InternalAlignment(g21,g24)
    c: InternalAlignment(g22,g24)
    c: InternalAlignment(g23,g24)
    c: InternalAlignment(g25,g24)
    c: InternalAlignment(g26,g24)
    c: Weight(g27) = 1
    c: Equal(g27,g28)
    c: Equal(g27,g29)
    c: Coincident(g30,g14)
    c: InternalAlignment(g27,g30)
    c: InternalAlignment(g28,g30)
    c: InternalAlignment(g29,g30)
    c: InternalAlignment(g31,g30)
    c: InternalAlignment(g32,g30)
    c: Coincident(g36,g12)
    c: Weight(g33) = 1
    c: Equal(g33,g34)
    c: Equal(g33,g35)
    c: Coincident(g36,g11)
    c: InternalAlignment(g33,g36)
    c: InternalAlignment(g34,g36)
    c: InternalAlignment(g35,g36)
    c: InternalAlignment(g37,g36)
    c: InternalAlignment(g38,g36)
    c: Coincident(g42,g13)
    c: Weight(g39) = 1
    c: Equal(g39,g40)
    c: Equal(g39,g41)
    c: Coincident(g42,g1)
    c: InternalAlignment(g39,g42)
    c: InternalAlignment(g40,g42)
    c: InternalAlignment(g41,g42)
    c: InternalAlignment(g43,g42)
    c: InternalAlignment(g44,g42)
    c: Block(g18)
    c: Block(g24)
    c: Block(g30)
    c: Block(g36)
    c: Block(g42)
    c: Horizontal(g45)
    c: Coincident(g45,g0)
    c: Vertical(g46)
    c: Coincident(g46,g45)
    c: Coincident(g47,g46)
    c: Coincident(g47,g18)
    c: Horizontal(g47)
    c: Block(g46)
    c: Coincident(g48,g18)
    c: Horizontal(g48)
    c: Distance(g48) = 1.33
    c: Vertical(g49)
    c: Coincident(g49,g48)
    c: Coincident(g50,g49)
    c: Coincident(g50,g24)
    c: Horizontal(g50)
    c: Tangent(g50,g22)
    c: Horizontal(g51)
    c: Coincident(g51,g24)
    c: Block(g51)
    c: Vertical(g52)
    c: Block(g52)
    c: Coincident(g52,g51)
    c: Coincident(g53,g52)
    c: Coincident(g53,g30)
    c: Horizontal(g53)
    c: Distance(g1) = 8.5
FEATURE [Part::Feature] Face024
  shape: bbox 9.8 x 26.5 x 2e-07 mm, 1 faces, 0 solids (baked)
FEATURE [Part::Revolution] Revolve024
  Angle = 360
  Axis = (0,1,0)
  Base = (0,0,0)
  FaceMakerClass = Part::FaceMakerBullseye
  Placement = pos=(0,0,0) rot=(0,0,1;1.5708rad)
  Solid = false
  Source = -> Face024
  Symmetric = false
FEATURE [Part::Feature] Face025
  shape: bbox 9.8 x 26.5 x 2e-07 mm, 1 faces, 0 solids (baked)
FEATURE [Part::Revolution] Revolve025
  Angle = 360
  Axis = (0,1,0)
  Base = (0,0,0)
  FaceMakerClass = Part::FaceMakerBullseye
  Placement = pos=(0,0,0) rot=(0,0,1;1.5708rad)
  Solid = false
  Source = -> Face025
  Symmetric = false
FEATURE [Part::MultiFuse] Fusion033
  Placement = pos=(-18,19,36) rot=(0,0,1;0rad)
  Shapes = -> [Revolve025,Revolve024]
FEATURE [Part::Cylinder] Cylinder014
  Angle = 360
  AttacherType = Attacher::AttachEngine3D
  Height = 20
  Placement = pos=(0,0,36.15) rot=(0,0,1;0rad)
  Radius = 14.3
FEATURE [Part::Cylinder] Cylinder015
  Angle = 360
  AttacherType = Attacher::AttachEngine3D
  Height = 10
  Placement = pos=(0,0,36.15) rot=(0,0,1;0rad)
  Radius = 4
FEATURE [Part::MultiFuse] Fusion034  label="removeToCreteHoleForPlugHousing004"
  Placement = pos=(-42,19,36) rot=(0,1,0;1.5708rad)
  Shapes = -> [Cylinder014,Cylinder015]
FEATURE [Part::Cut] Cut008  label="top004"
  Base = -> Cut004
  Placement = pos=(-1,0,0) rot=(0,0,1;0rad)
  Tool = -> Fusion034
FEATURE [Part::Box] Box005  label="Cube005"
  AttacherType = Attacher::AttachEngine3D
  Height = 28
  Length = 3
  Placement = pos=(110.7,19,22) rot=(0,0,1;0rad)
  Width = 15.7
FEATURE [Part::Cylinder] Cylinder016
  Angle = 360
  AttacherType = Attacher::AttachEngine3D
  Height = 10
  Placement = pos=(0,0,36.15) rot=(0,0,1;0rad)
  Radius = 4
FEATURE [Part::Cylinder] Cylinder017
  Angle = 360
  AttacherType = Attacher::AttachEngine3D
  Height = 20
  Placement = pos=(0,0,36.15) rot=(0,0,1;0rad)
  Radius = 10.3
FEATURE [Part::MultiFuse] Fusion035  label="removeToCreteHoleForPlugHousing005"
  Placement = pos=(70,19,36) rot=(0,1,0;1.5708rad)
  Shapes = -> [Cylinder017,Cylinder016]
FEATURE [Part::Cut] Cut009  label="plugHousingTab001"
  Base = -> Box005
  Placement = pos=(-107.4,-14,0) rot=(0,0,1;0rad)
  Tool = -> Fusion035
FEATURE [Part::Box] Box006  label="Cube006"
  AttacherType = Attacher::AttachEngine3D
  Height = 28
  Length = 3
  Placement = pos=(110.7,19,22) rot=(0,0,1;0rad)
  Width = 15.7
FEATURE [Part::Cylinder] Cylinder018
  Angle = 360
  AttacherType = Attacher::AttachEngine3D
  Height = 10
  Placement = pos=(0,0,36.15) rot=(0,0,1;0rad)
  Radius = 4
FEATURE [Part::Cylinder] Cylinder019
  Angle = 360
  AttacherType = Attacher::AttachEngine3D
  Height = 20
  Placement = pos=(0,0,36.15) rot=(0,0,1;0rad)
  Radius = 10.3
FEATURE [Part::MultiFuse] Fusion036  label="removeToCreteHoleForPlugHousing006"
  Placement = pos=(70,19,36) rot=(0,1,0;1.5708rad)
  Shapes = -> [Cylinder019,Cylinder018]
FEATURE [Part::Cut] Cut010  label="plugHousingTab002"
  Base = -> Box006
  Placement = pos=(-107.4,-14,0) rot=(0,0,1;0rad)
  Tool = -> Fusion036
FEATURE [Part::MultiFuse] Fusion037
  Placement = pos=(9.6,23,0) rot=(0,0,1;3.14159rad)
  Shapes = -> [Cut009,Cut010]
FEATURE [Part::Box] Box  label="Cube"
  AttacherType = Attacher::AttachEngine3D
  Height = 10
  Length = 3
  Placement = pos=(3.3,4,12) rot=(0,0,1;0rad)
  Width = 10
FEATURE [Part::Fillet] Fillet004
  Base = -> Fusion028
  Edges = 1 edges r=2: [Edge25]
FEATURE [Part::Fillet] Fillet005  label="plugHousing046"
  Base = -> Fillet004
  Edges = 1 edges r=2: [Edge8]
FEATURE [Part::Fillet] Fillet006
  Base = -> Box
  Edges = 1 edges r=2: [Edge11]
FEATURE [Part::Box] Box007  label="Cube007"
  AttacherType = Attacher::AttachEngine3D
  Height = 10
  Length = 3
  Placement = pos=(3.3,4,50) rot=(0,0,1;0rad)
  Width = 10
FEATURE [Part::Fillet] Fillet007
  Base = -> Box007
  Edges = 1 edges r=2: [Edge12]
FEATURE [Part::Box] Box008  label="Cube008"
  AttacherType = Attacher::AttachEngine3D
  Height = 28
  Length = 4
  Placement = pos=(5,0,22) rot=(0,0,1;0rad)
  Width = 10
FEATURE [Part::Fillet] Fillet008
  Base = -> Box008
  Edges = 1 edges r=1: [Edge7]
FEATURE [Part::Fillet] Fillet009
  Base = -> Fillet008
  Edges = 1 edges r=2: [Edge5]
FEATURE [Part::Fillet] Fillet010
  Base = -> Fillet009
  Edges = 1 edges r=2: [Edge2]
FEATURE [Sketcher::SketchObject] Sketch009  label="topSketch003"
  FullyConstrained = true
  sketch-geometry (4):
    g0: LineSegment StartX=16.8446 StartY=31.512 StartZ=0 EndX=16.3251 EndY=34.4666 EndZ=0
    g1: ArcOfCircle CenterX=19 CenterY=19.2524 CenterZ=0 NormalX=0 NormalY=0 NormalZ=1 AngleXU=0 Radius=15.4476 StartAngle=1.74483 EndAngle=2.72717
    g2: ArcOfCircle CenterX=19 CenterY=19.2524 CenterZ=0 NormalX=0 NormalY=0 NormalZ=1 AngleXU=0 Radius=12.4476 StartAngle=1.74483 EndAngle=2.73189
    g3: LineSegment StartX=4.86004 StartY=25.4725 StartZ=0 EndX=7.58253 EndY=24.2107 EndZ=0
  constraints (7):
    c: Block(g0)
    c: Coincident(g1,g0)
    c: Coincident(g2,g0)
    c: Coincident(g3,g1)
    c: Coincident(g3,g2)
    c: Block(g1)
    c: Block(g2)
FEATURE [Part::Extrusion] Extrude008
  Base = -> Sketch009
  Dir = (0,0,1)
  DirMode = 2
  FaceMakerClass = Part::FaceMakerBullseye
  LengthFwd = 10
  LengthRev = 0
  Placement = pos=(0,0,31) rot=(0,0,1;0rad)
  Solid = true
  Symmetric = false
FEATURE [Part::Cylinder] Cylinder020
  Angle = 360
  AttacherType = Attacher::AttachEngine3D
  Height = 20
  Placement = pos=(0,0,36.15) rot=(0,0,1;0rad)
  Radius = 8.2
FEATURE [Part::Cylinder] Cylinder021
  Angle = 360
  AttacherType = Attacher::AttachEngine3D
  Height = 10
  Placement = pos=(0,0,36.15) rot=(0,0,1;0rad)
  Radius = 4
FEATURE [Part::MultiFuse] Fusion038  label="removeToCreteHoleForPlugHousing007"
  Placement = pos=(-42,19,36) rot=(0,1,0;1.5708rad)
  Shapes = -> [Cylinder020,Cylinder021]
FEATURE [Part::Cut] Cut011
  Base = -> Extrude008
  Tool = -> Fusion038
FEATURE [Part::Fillet] Fillet011
  Base = -> Cut011
  Edges = 1 edges r=2: [Edge1]
FEATURE [Part::Fillet] Fillet012
  Base = -> Fillet011
  Edges = 1 edges r=2.5: [Edge1]
FEATURE [Part::Fillet] Fillet013
  Base = -> Fillet012
  Edges = 1 edges r=2.5: [Edge2]
FEATURE [Part::Box] Box010  label="Cube010"
  AttacherType = Attacher::AttachEngine3D
  Height = 16
  Length = 8
  Placement = pos=(12.7,31.52,28) rot=(0,0,1;0rad)
  Width = 4
FEATURE [Sketcher::SketchObject] Sketch010  label="topSketch004"
  FullyConstrained = true
  sketch-geometry (4):
    g0: LineSegment StartX=16.8446 StartY=31.512 StartZ=0 EndX=16.3251 EndY=34.4666 EndZ=0
    g1: ArcOfCircle CenterX=19 CenterY=19.2524 CenterZ=0 NormalX=0 NormalY=0 NormalZ=1 AngleXU=0 Radius=15.4476 StartAngle=1.74483 EndAngle=2.72717
    g2: ArcOfCircle CenterX=19 CenterY=19.2524 CenterZ=0 NormalX=0 NormalY=0 NormalZ=1 AngleXU=0 Radius=12.4476 StartAngle=1.74483 EndAngle=2.73189
    g3: LineSegment StartX=4.86004 StartY=25.4725 StartZ=0 EndX=7.58253 EndY=24.2107 EndZ=0
  constraints (7):
    c: Block(g0)
    c: Coincident(g1,g0)
    c: Coincident(g2,g0)
    c: Coincident(g3,g1)
    c: Coincident(g3,g2)
    c: Block(g1)
    c: Block(g2)
FEATURE [Part::Cylinder] Cylinder022
  Angle = 360
  AttacherType = Attacher::AttachEngine3D
  Height = 10
  Placement = pos=(0,0,36.15) rot=(0,0,1;0rad)
  Radius = 4
FEATURE [Sketcher::SketchObject] Sketch011  label="topSketch005"
  FullyConstrained = true
  sketch-geometry (4):
    g0: LineSegment StartX=16.8446 StartY=31.512 StartZ=0 EndX=16.3251 EndY=34.4666 EndZ=0
    g1: ArcOfCircle CenterX=19 CenterY=19.2524 CenterZ=0 NormalX=0 NormalY=0 NormalZ=1 AngleXU=0 Radius=15.4476 StartAngle=1.74483 EndAngle=2.72717
    g2: ArcOfCircle CenterX=19 CenterY=19.2524 CenterZ=0 NormalX=0 NormalY=0 NormalZ=1 AngleXU=0 Radius=12.4476 StartAngle=1.74483 EndAngle=2.73189
    g3: LineSegment StartX=4.86004 StartY=25.4725 StartZ=0 EndX=7.58253 EndY=24.2107 EndZ=0
  constraints (7):
    c: Block(g0)
    c: Coincident(g1,g0)
    c: Coincident(g2,g0)
    c: Coincident(g3,g1)
    c: Coincident(g3,g2)
    c: Block(g1)
    c: Block(g2)
FEATURE [Part::Extrusion] Extrude010
  Base = -> Sketch011
  Dir = (0,0,1)
  DirMode = 2
  FaceMakerClass = Part::FaceMakerBullseye
  LengthFwd = 10.6
  LengthRev = 0
  Placement = pos=(0,0,31) rot=(0,0,1;0rad)
  Solid = true
  Symmetric = false
FEATURE [Part::Cylinder] Cylinder023
  Angle = 360
  AttacherType = Attacher::AttachEngine3D
  Height = 20
  Placement = pos=(0,0,36.15) rot=(0,0,1;0rad)
  Radius = 8.2
FEATURE [Part::MultiFuse] Fusion039  label="removeToCreteHoleForPlugHousing008"
  Placement = pos=(-42,19,36) rot=(0,1,0;1.5708rad)
  Shapes = -> [Cylinder023,Cylinder022]
FEATURE [Part::Cut] Cut012
  Base = -> Extrude010
  Placement = pos=(0,0,-0.3) rot=(0,0,1;0rad)
  Tool = -> Fusion039
FEATURE [Part::Cut] Cut013
  Base = -> Box010
  Tool = -> Cut012
FEATURE [Part::Fillet] Fillet014
  Base = -> Cut013
  Edges = 1 edges r=0.7: [Edge13]
FEATURE [Part::Fillet] Fillet015
  Base = -> Fillet014
  Edges = 1 edges r=0.7: [Edge13]
FEATURE [Part::Fillet] Fillet016
  Base = -> Fillet015
  Edges = 1 edges r=0.7: [Edge16]
FEATURE [Part::Fillet] Fillet017
  Base = -> Fillet016
  Edges = 1 edges r=0.7: [Edge11]
FEATURE [Part::Fillet] Fillet018
  Base = -> Fillet017
  Edges = 1 edges r=0.7: [Edge10]
FEATURE [Part::Fillet] Fillet019
  Base = -> Fillet018
  Edges = 1 edges r=1.2: [Edge5]
FEATURE [Part::Fillet] Fillet020
  Base = -> Fillet019
  Edges = 1 edges r=1.2: [Edge12]
FEATURE [Part::Fillet] Fillet021
  Base = -> Fillet020
  Edges = 1 edges r=2: [Edge1]
  Placement = pos=(0.3,0,0) rot=(0,0,1;0rad)
FEATURE [Part::MultiFuse] Fusion040  label="top005"
  Shapes = -> [Cut008,Fillet021]
FEATURE [Part::MultiFuse] Fusion041  label="wireHolder"
  Shapes = -> [Fusion033,Fillet013]
FEATURE [Part::MultiFuse] Fusion042
  Shapes = -> [Fillet007,Fusion041]
FEATURE [Part::MultiFuse] Fusion043  label="wireHolder001"
  Shapes = -> [Fusion042,Fillet010]
FEATURE [Part::MultiFuse] Fusion044  label="wireHolder002"
  Shapes = -> [Fillet006,Fusion037,Fusion043]
FEATURE [Part::Feature] Face026
  shape: bbox 11 x 6 x 2e-07 mm, 1 faces, 0 solids (baked)
FEATURE [Part::Revolution] Revolve026
  Angle = 360
  Axis = (0,1,0)
  Base = (0,0,0)
  FaceMakerClass = Part::FaceMakerBullseye
  Placement = pos=(30.3,-1,19.7) rot=(0,0,1;0rad)
  Solid = false
  Source = -> Face026
  Symmetric = false
FEATURE [Sketcher::SketchObject] Sketch013  label="topSketch006"
  FullyConstrained = true
  sketch-geometry (13):
    g0: LineSegment StartX=117 StartY=19 StartZ=0 EndX=117 EndY=38 EndZ=0
    g1: ArcOfCircle CenterX=98 CenterY=19 CenterZ=0 NormalX=0 NormalY=0 NormalZ=1 AngleXU=0 Radius=19 StartAngle=5.7297 EndAngle=6.28319
    g2: LineSegment StartX=0 StartY=3 StartZ=0 EndX=0 EndY=19 EndZ=0
    g3: LineSegment StartX=19 StartY=38 StartZ=0 EndX=117 EndY=38 EndZ=0
    g4: ArcOfCircle CenterX=19 CenterY=19 CenterZ=0 NormalX=0 NormalY=0 NormalZ=1 AngleXU=0 Radius=19 StartAngle=1.5708 EndAngle=3.14159
    g5: ArcOfCircle CenterX=19 CenterY=19 CenterZ=0 NormalX=0 NormalY=0 NormalZ=1 AngleXU=0 Radius=16 StartAngle=1.5708 EndAngle=3.14159
    g6: ArcOfCircle CenterX=98 CenterY=19 CenterZ=0 NormalX=0 NormalY=0 NormalZ=1 AngleXU=0 Radius=16 StartAngle=5.60905 EndAngle=6.28319
    g7: LineSegment StartX=114 StartY=19 StartZ=0 EndX=114 EndY=35 EndZ=0
    g8: LineSegment StartX=110.5 StartY=9.01251 StartZ=0 EndX=114.163 EndY=9.01251 EndZ=0
    g9: LineSegment StartX=114 StartY=35 StartZ=0 EndX=19 EndY=35 EndZ=0
    g10: LineSegment StartX=0 StartY=3 StartZ=0 EndX=0 EndY=0 EndZ=0
    g11: LineSegment StartX=3 StartY=0 StartZ=0 EndX=0 EndY=0 EndZ=0
    g12: LineSegment StartX=3 StartY=19 StartZ=0 EndX=3 EndY=0 EndZ=0
  constraints (33):
    c: Vertical(g0)
    c: Distance(g0) = 19
    c: Block(g0)
    c: Coincident(g1,g0)
    c: Block(g1)
    c: Vertical(g2)
    c: Block(g2)
    c: Coincident(g3,g0)
    c: Horizontal(g3)
    c: Distance(g3) = 98
    c: Coincident(g4,g3)
    c: Coincident(g4,g2)
    c: Block(g4)
    c: Coincident(g5,g4)
    c: Coincident(g6,g1)
    c: Block(g6)
    c: Block(g5)
    c: Coincident(g7,g6)
    c: Vertical(g7)
    c: Coincident(g8,g6)
    c: Coincident(g8,g1)
    c: Coincident(g9,g7)
    c: Coincident(g9,g5)
    c: Horizontal(g9)
    c: Tangent(g9,g5)
    c: Coincident(g10,g2)
    c: Distance(g10) = 3
    c: Vertical(g10)
    c: Coincident(g11,g10)
    c: Horizontal(g11)
    c: Coincident(g12,g5)
    c: Coincident(g12,g11)
    c: Vertical(g12)
FEATURE [Part::Extrusion] Extrude011  label="top006"
  Base = -> Sketch013
  Dir = (0,0,1)
  DirMode = 2
  FaceMakerClass = Part::FaceMakerBullseye
  LengthFwd = 72
  LengthRev = 0
  Solid = true
  Symmetric = false
FEATURE [Sketcher::SketchObject] Sketch014
  FullyConstrained = true
  MapMode = 3
  Placement = pos=(0,0,0) rot=(1,0,0;1.5708rad)
  Support = -> [Extrude011]
  sketch-geometry (8):
    g0: Circle CenterX=80.351 CenterY=-67.6202 CenterZ=0 NormalX=0 NormalY=0 NormalZ=1 AngleXU=0 Radius=2
    g1: Circle CenterX=80.351 CenterY=-67.6202 CenterZ=0 NormalX=0 NormalY=0 NormalZ=1 AngleXU=0 Radius=3
    g2: Circle CenterX=80.351 CenterY=-4.92017 CenterZ=0 NormalX=0 NormalY=0 NormalZ=1 AngleXU=0 Radius=2
    g3: Circle CenterX=80.351 CenterY=-4.92017 CenterZ=0 NormalX=0 NormalY=0 NormalZ=1 AngleXU=0 Radius=3
    g4: Circle CenterX=23.851 CenterY=-4.92017 CenterZ=0 NormalX=0 NormalY=0 NormalZ=1 AngleXU=0 Radius=2
    g5: Circle CenterX=23.851 CenterY=-4.92017 CenterZ=0 NormalX=0 NormalY=0 NormalZ=1 AngleXU=0 Radius=3
    g6: Circle CenterX=23.851 CenterY=-67.6202 CenterZ=0 NormalX=0 NormalY=0 NormalZ=1 AngleXU=0 Radius=2
    g7: Circle CenterX=23.851 CenterY=-67.6202 CenterZ=0 NormalX=0 NormalY=0 NormalZ=1 AngleXU=0 Radius=3
  constraints (8):
    c: Block(g3)
    c: Block(g2)
    c: Block(g1)
    c: Block(g0)
    c: Block(g6)
    c: Block(g7)
    c: Block(g4)
    c: Block(g5)
FEATURE [Part::Feature] Face027
  shape: bbox 11 x 6 x 2e-07 mm, 1 faces, 0 solids (baked)
FEATURE [Part::Revolution] Revolve027
  Angle = 360
  Axis = (0,1,0)
  Base = (0,0,0)
  FaceMakerClass = Part::FaceMakerBullseye
  Placement = pos=(30.3,-1,51.7) rot=(0,0,1;0rad)
  Solid = false
  Source = -> Face027
  Symmetric = false
FEATURE [Part::Feature] Face028
  shape: bbox 11 x 6 x 2e-07 mm, 1 faces, 0 solids (baked)
FEATURE [Part::Revolution] Revolve028
  Angle = 360
  Axis = (0,1,0)
  Base = (0,0,0)
  FaceMakerClass = Part::FaceMakerBullseye
  Placement = pos=(62.3,-1,19.7) rot=(0,0,1;0rad)
  Solid = false
  Source = -> Face028
  Symmetric = false
FEATURE [Part::Feature] Face029
  shape: bbox 11 x 6 x 2e-07 mm, 1 faces, 0 solids (baked)
FEATURE [Part::Revolution] Revolve029
  Angle = 360
  Axis = (0,1,0)
  Base = (0,0,0)
  FaceMakerClass = Part::FaceMakerBullseye
  Placement = pos=(62.3,-1,51.7) rot=(0,0,1;0rad)
  Solid = false
  Source = -> Face029
  Symmetric = false
FEATURE [Part::Feature] Wire
  shape: bbox 11 x 5.2 x 2e-07 mm, 0 faces, 0 solids (baked)
FEATURE [Part::Revolution] Revolve030
  Angle = 360
  Axis = (0,1,0)
  Base = (0,0,0)
  FaceMakerClass = Part::FaceMakerBullseye
  Placement = pos=(30.3,38,19.7) rot=(0,0,1;0rad)
  Solid = true
  Source = -> Wire
  Symmetric = false
FEATURE [Part::Feature] Wire001
  shape: bbox 11 x 5.2 x 2e-07 mm, 0 faces, 0 solids (baked)
FEATURE [Part::Revolution] Revolve031
  Angle = 360
  Axis = (0,1,0)
  Base = (0,0,0)
  FaceMakerClass = Part::FaceMakerBullseye
  Placement = pos=(30.3,38,51.7) rot=(0,0,1;0rad)
  Solid = true
  Source = -> Wire001
  Symmetric = false
FEATURE [Part::Feature] Wire002
  shape: bbox 11 x 5.2 x 2e-07 mm, 0 faces, 0 solids (baked)
FEATURE [Part::Revolution] Revolve032
  Angle = 360
  Axis = (0,1,0)
  Base = (0,0,0)
  FaceMakerClass = Part::FaceMakerBullseye
  Placement = pos=(62.3,38,51.7) rot=(0,0,1;0rad)
  Solid = true
  Source = -> Wire002
  Symmetric = false
FEATURE [Part::Feature] Wire003
  shape: bbox 11 x 5.2 x 2e-07 mm, 0 faces, 0 solids (baked)
FEATURE [Part::Revolution] Revolve033
  Angle = 360
  Axis = (0,1,0)
  Base = (0,0,0)
  FaceMakerClass = Part::FaceMakerBullseye
  Placement = pos=(62.3,38,19.7) rot=(0,0,1;0rad)
  Solid = true
  Source = -> Wire003
  Symmetric = false
FEATURE [Part::MultiFuse] Fusion045  label="altRandScrewHousing"
  Shapes = -> [Revolve029,Revolve027,Revolve028,Revolve026]
FEATURE [Part::MultiFuse] Fusion046  label="fanScrewHousing"
  Shapes = -> [Revolve033,Revolve032,Revolve031,Revolve030]
FEATURE [Sketcher::SketchObject] Sketch015
  FullyConstrained = true
  sketch-geometry (17):
    g0: Circle CenterX=-3.5 CenterY=23.5 CenterZ=0 NormalX=0 NormalY=0 NormalZ=1 AngleXU=0 Radius=1
    g1: Circle CenterX=-1 CenterY=15.25 CenterZ=0 NormalX=0 NormalY=0 NormalZ=1 AngleXU=0 Radius=1
    g2: Circle CenterX=-3.5 CenterY=7 CenterZ=0 NormalX=0 NormalY=0 NormalZ=1 AngleXU=0 Radius=1
    g3: BSplineCurve PolesCount=3 KnotsCount=2 Degree=2 IsPeriodic=0
    g4: GeomPoint X=-3.5 Y=23.5 Z=0
    g5: GeomPoint X=-3.5 Y=7 Z=0
    g6: Circle CenterX=-4.8 CenterY=30.5 CenterZ=0 NormalX=0 NormalY=0 NormalZ=1 AngleXU=0 Radius=1
    g7: Circle CenterX=-3.5 CenterY=30.5 CenterZ=0 NormalX=0 NormalY=0 NormalZ=1 AngleXU=0 Radius=1
    g8: Circle CenterX=-3.5 CenterY=29.2 CenterZ=0 NormalX=0 NormalY=0 NormalZ=1 AngleXU=0 Radius=1
    g9: BSplineCurve PolesCount=3 KnotsCount=2 Degree=2 IsPeriodic=0
    g10: GeomPoint X=-4.8 Y=30.5 Z=0
    g11: GeomPoint X=-3.5 Y=29.2 Z=0
    g12: LineSegment StartX=-3.5 StartY=29.2 StartZ=0 EndX=-3.5 EndY=23.5 EndZ=0
    g13: LineSegment StartX=-4.8 StartY=30.5 StartZ=0 EndX=0 EndY=30.5 EndZ=0
    g14: LineSegment StartX=-3.5 StartY=0.3 StartZ=0 EndX=0 EndY=0.3 EndZ=0
    g15: LineSegment StartX=-3.5 StartY=0.3 StartZ=0 EndX=-3.5 EndY=7 EndZ=0
    g16: LineSegment StartX=0 StartY=0.3 StartZ=0 EndX=0 EndY=30.5 EndZ=0
  constraints (33):
    c: Weight(g0) = 1
    c: Equal(g0,g1)
    c: Equal(g0,g2)
    c: InternalAlignment(g0,g3)
    c: InternalAlignment(g1,g3)
    c: InternalAlignment(g2,g3)
    c: InternalAlignment(g4,g3)
    c: InternalAlignment(g5,g3)
    c: Block(g3)
    c: Weight(g6) = 1
    c: Equal(g6,g7)
    c: Equal(g6,g8)
    c: InternalAlignment(g6,g9)
    c: InternalAlignment(g7,g9)
    c: InternalAlignment(g8,g9)
    c: InternalAlignment(g10,g9)
    c: InternalAlignment(g11,g9)
    c: Block(g9)
    c: Coincident(g12,g9)
    c: Coincident(g12,g3)
    c: Vertical(g12)
    c: Coincident(g13,g9)
    c: Horizontal(g13)
    c: Distance(g13) = 4.8
    c: Horizontal(g14)
    c: Block(g14)
    c: Coincident(g15,g14)
    c: Coincident(g15,g3)
    c: Vertical(g15)
    c: Coincident(g16,g14)
    c: Coincident(g16,g13)
    c: Vertical(g16)
    c: Tangent(g16,g1)
FEATURE [Sketcher::SketchObject] Sketch016
  FullyConstrained = true
  sketch-geometry (16):
    g0: Circle CenterX=-3.5 CenterY=23.5 CenterZ=0 NormalX=0 NormalY=0 NormalZ=1 AngleXU=0 Radius=1
    g1: Circle CenterX=-1 CenterY=15.25 CenterZ=0 NormalX=0 NormalY=0 NormalZ=1 AngleXU=0 Radius=1
    g2: Circle CenterX=-3.5 CenterY=7 CenterZ=0 NormalX=0 NormalY=0 NormalZ=1 AngleXU=0 Radius=1
    g3: BSplineCurve PolesCount=3 KnotsCount=2 Degree=2 IsPeriodic=0
    g4: GeomPoint X=-3.5 Y=23.5 Z=0
    g5: GeomPoint X=-3.5 Y=7 Z=0
    g6: LineSegment StartX=-3.5 StartY=28.2 StartZ=0 EndX=-3.5 EndY=23.5 EndZ=0
    g7: LineSegment StartX=0 StartY=29.5 StartZ=0 EndX=0 EndY=30 EndZ=0
    g8: LineSegment StartX=-3.5 StartY=28.2 StartZ=0 EndX=-3.5 EndY=30 EndZ=0
    g9: LineSegment StartX=0 StartY=30 StartZ=0 EndX=0 EndY=30.5 EndZ=0
    g10: LineSegment StartX=0 StartY=30.5 StartZ=0 EndX=-3.5 EndY=30.5 EndZ=0
    g11: LineSegment StartX=-3.5 StartY=30.5 StartZ=0 EndX=-3.5 EndY=30 EndZ=0
    g12: LineSegment StartX=0 StartY=29.5 StartZ=0 EndX=0 EndY=5 EndZ=0
    g13: LineSegment StartX=-3.5 StartY=0.3 StartZ=0 EndX=-3.5 EndY=7 EndZ=0
    g14: LineSegment StartX=-3.5 StartY=0.3 StartZ=0 EndX=0 EndY=0.3 EndZ=0
    g15: LineSegment StartX=0 StartY=5 StartZ=0 EndX=0 EndY=0.3 EndZ=0
  constraints (39):
    c: Weight(g0) = 1
    c: Equal(g0,g1)
    c: Equal(g0,g2)
    c: InternalAlignment(g0,g3)
    c: InternalAlignment(g1,g3)
    c: InternalAlignment(g2,g3)
    c: InternalAlignment(g4,g3)
    c: InternalAlignment(g5,g3)
    c: Block(g3)
    c: Coincident(g6,g3)
    c: Vertical(g6)
    c: Vertical(g7)
    c: Distance(g7) = 0.5
    c: Coincident(g8,g6)
    c: Vertical(g8)
    c: Block(g6)
    c: Block(g7)
    c: Vertical(g9)
    c: Equal(g7,g9) = 0.5
    c: Block(g9)
    c: Coincident(g9,g7)
    c: Horizontal(g10)
    c: Coincident(g10,g9)
    c: Coincident(g11,g10)
    c: Coincident(g11,g8)
    c: Vertical(g11)
    c: Block(g11)
    c: Coincident(g12,g7)
    c: Vertical(g12)
    c: Coincident(g13,g3)
    c: Vertical(g13)
    c: Distance(g13) = 6.7
    c: Coincident(g14,g13)
    c: Horizontal(g14)
    c: Block(g14)
    c: Coincident(g15,g12)
    c: Coincident(g15,g14)
    c: Vertical(g15)
    c: Block(g15)
FEATURE [Sketcher::SketchObject] Sketch017
  FullyConstrained = true
  sketch-geometry (11):
    g0: LineSegment StartX=-3.5 StartY=1e-16 StartZ=0 EndX=-1.6 EndY=1e-16 EndZ=0
    g1: LineSegment StartX=-1.6 StartY=1e-16 StartZ=0 EndX=-1.6 EndY=1.5 EndZ=0
    g2: LineSegment StartX=-3.5 StartY=1.5 StartZ=0 EndX=-1.6 EndY=1.5 EndZ=0
    g3: LineSegment StartX=-3.5 StartY=1e-16 StartZ=0 EndX=-4.8 EndY=1e-16 EndZ=0
    g4: Circle CenterX=-3.5 CenterY=1.3 CenterZ=0 NormalX=0 NormalY=0 NormalZ=1 AngleXU=0 Radius=1
    g5: Circle CenterX=-3.5 CenterY=1e-16 CenterZ=0 NormalX=0 NormalY=0 NormalZ=1 AngleXU=0 Radius=1
    g6: Circle CenterX=-4.8 CenterY=1e-16 CenterZ=0 NormalX=0 NormalY=0 NormalZ=1 AngleXU=0 Radius=1
    g7: BSplineCurve PolesCount=3 KnotsCount=2 Degree=2 IsPeriodic=0
    g8: GeomPoint X=-3.5 Y=1.3 Z=0
    g9: GeomPoint X=-4.8 Y=1e-16 Z=0
    g10: LineSegment StartX=-3.5 StartY=1.3 StartZ=0 EndX=-3.5 EndY=1.5 EndZ=0
  constraints (24):
    c: Horizontal(g0)
    c: Distance(g0) = 1.9
    c: Block(g0)
    c: Coincident(g1,g0)
    c: Vertical(g1)
    c: Coincident(g2,g1)
    c: Horizontal(g2)
    c: Coincident(g3,g0)
    c: Horizontal(g3)
    c: Distance(g3) = 1.3
    c: Weight(g4) = 1
    c: Equal(g4,g5)
    c: Coincident(g5,g0)
    c: Equal(g4,g6)
    c: Coincident(g7,g3)
    c: InternalAlignment(g4,g7)
    c: InternalAlignment(g5,g7)
    c: InternalAlignment(g6,g7)
    c: InternalAlignment(g8,g7)
    c: InternalAlignment(g9,g7)
    c: Coincident(g10,g7)
    c: Coincident(g10,g2)
    c: Vertical(g10)
    c: Block(g10)
FEATURE [Part::Feature] Face035
  shape: bbox 3.2 x 1.5 x 2e-07 mm, 1 faces, 0 solids (baked)
FEATURE [Part::Revolution] Revolve039  label="backCaseScrewRetainer"
  Angle = 360
  Axis = (0,1,0)
  Base = (0,0,0)
  FaceMakerClass = Part::FaceMakerBullseye
  Placement = pos=(12.5,3,62) rot=(0,0,1;0rad)
  Solid = false
  Source = -> Face035
  Symmetric = false
FEATURE [Part::Feature] Face036
  shape: bbox 3.2 x 1.5 x 2e-07 mm, 1 faces, 0 solids (baked)
FEATURE [Part::Feature] Face039
  shape: bbox 4.8 x 30.2 x 2e-07 mm, 1 faces, 0 solids (baked)
FEATURE [Part::Revolution] Revolve043  label="frontCaseScrewPost002"
  Angle = 360
  Axis = (0,1,0)
  Base = (0,0,0)
  FaceMakerClass = Part::FaceMakerBullseye
  Placement = pos=(89.5,4.5,3.5) rot=(0,0,1;0rad)
  Solid = false
  Source = -> Face039
  Symmetric = false
FEATURE [Part::Feature] Face042
  shape: bbox 4.8 x 30.2 x 2e-07 mm, 1 faces, 0 solids (baked)
FEATURE [Part::Revolution] Revolve046  label="frontCaseScrewPost003"
  Angle = 360
  Axis = (0,1,0)
  Base = (0,0,0)
  FaceMakerClass = Part::FaceMakerBullseye
  Placement = pos=(89.5,4.5,68.5) rot=(0,0,1;0rad)
  Solid = false
  Source = -> Face042
  Symmetric = false
FEATURE [Part::Feature] Face043
  shape: bbox 3.2 x 1.5 x 2e-07 mm, 1 faces, 0 solids (baked)
FEATURE [Part::Revolution] Revolve047  label="frontCaseScrewRetainer002"
  Angle = 360
  Axis = (0,1,0)
  Base = (0,0,0)
  FaceMakerClass = Part::FaceMakerBullseye
  Placement = pos=(89.5,3,68.5) rot=(0,0,1;0rad)
  Solid = false
  Source = -> Face043
  Symmetric = false
FEATURE [Part::Feature] Face044
  shape: bbox 3.2 x 1.5 x 2e-07 mm, 1 faces, 0 solids (baked)
FEATURE [Part::Revolution] Revolve048  label="frontCaseScrewRetainer003"
  Angle = 360
  Axis = (0,1,0)
  Base = (0,0,0)
  FaceMakerClass = Part::FaceMakerBullseye
  Placement = pos=(89.5,3,3.5) rot=(0,0,1;0rad)
  Solid = false
  Source = -> Face044
  Symmetric = false
FEATURE [App::MeasureDistance] Distance002  label="Distance: 1.67 mm"
  Distance = 1.66921
  P1 = (99.2361,4.7524,71.7)
  P2 = (99.2347,6.42161,71.7)
FEATURE [Sketcher::SketchObject] Sketch018
  FullyConstrained = true
  sketch-geometry (7):
    g0: LineSegment StartX=0 StartY=0 StartZ=0 EndX=0 EndY=6 EndZ=0
    g1: Circle CenterX=0 CenterY=0 CenterZ=0 NormalX=0 NormalY=0 NormalZ=1 AngleXU=0 Radius=1
    g2: Circle CenterX=8 CenterY=6 CenterZ=0 NormalX=0 NormalY=0 NormalZ=1 AngleXU=0 Radius=1
    g3: BSplineCurve PolesCount=3 KnotsCount=2 Degree=2 IsPeriodic=0
    g4: GeomPoint X=0 Y=0 Z=0
    g5: GeomPoint X=8 Y=6 Z=0
    g6: LineSegment StartX=0 StartY=6 StartZ=0 EndX=8 EndY=6 EndZ=0
  constraints (14):
    c: Coincident(g0,g-1)
    c: Distance(g0) = 6
    c: Vertical(g0)
    c: Coincident(g3,g0)
    c: Weight(g1) = 1
    c: Equal(g1,g2)
    c: InternalAlignment(g1,g3)
    c: InternalAlignment(g2,g3)
    c: InternalAlignment(g4,g3)
    c: InternalAlignment(g5,g3)
    c: Block(g3)
    c: Coincident(g6,g0)
    c: Coincident(g6,g3)
    c: Horizontal(g6)
FEATURE [Part::Extrusion] Extrude012  label="caseScrewPillarBracket"
  Base = -> Sketch018
  Dir = (0,0,1)
  DirMode = 2
  FaceMakerClass = Part::FaceMakerBullseye
  LengthFwd = 2.4
  LengthRev = 0
  Placement = pos=(15.76,29,8.8) rot=(0,1,0;0rad)
  Solid = true
  Symmetric = false
FEATURE [Sketcher::SketchObject] Sketch019
  FullyConstrained = true
  sketch-geometry (7):
    g0: LineSegment StartX=0 StartY=0 StartZ=0 EndX=0 EndY=6 EndZ=0
    g1: Circle CenterX=0 CenterY=0 CenterZ=0 NormalX=0 NormalY=0 NormalZ=1 AngleXU=0 Radius=1
    g2: Circle CenterX=8 CenterY=6 CenterZ=0 NormalX=0 NormalY=0 NormalZ=1 AngleXU=0 Radius=1
    g3: BSplineCurve PolesCount=3 KnotsCount=2 Degree=2 IsPeriodic=0
    g4: GeomPoint X=0 Y=0 Z=0
    g5: GeomPoint X=8 Y=6 Z=0
    g6: LineSegment StartX=0 StartY=6 StartZ=0 EndX=8 EndY=6 EndZ=0
  constraints (14):
    c: Coincident(g0,g-1)
    c: Distance(g0) = 6
    c: Vertical(g0)
    c: Coincident(g3,g0)
    c: Weight(g1) = 1
    c: Equal(g1,g2)
    c: InternalAlignment(g1,g3)
    c: InternalAlignment(g2,g3)
    c: InternalAlignment(g4,g3)
    c: InternalAlignment(g5,g3)
    c: Block(g3)
    c: Coincident(g6,g0)
    c: Coincident(g6,g3)
    c: Horizontal(g6)
FEATURE [Part::Extrusion] Extrude013  label="caseScrewPillarBracket001"
  Base = -> Sketch019
  Dir = (0,0,1)
  DirMode = 2
  FaceMakerClass = Part::FaceMakerBullseye
  LengthFwd = 2.4
  LengthRev = 0
  Placement = pos=(15.76,29,60.8) rot=(0,0,1;0rad)
  Solid = true
  Symmetric = false
FEATURE [Sketcher::SketchObject] Sketch020
  FullyConstrained = true
  sketch-geometry (7):
    g0: LineSegment StartX=0 StartY=0 StartZ=0 EndX=0 EndY=6 EndZ=0
    g1: Circle CenterX=0 CenterY=0 CenterZ=0 NormalX=0 NormalY=0 NormalZ=1 AngleXU=0 Radius=1
    g2: Circle CenterX=8 CenterY=6 CenterZ=0 NormalX=0 NormalY=0 NormalZ=1 AngleXU=0 Radius=1
    g3: BSplineCurve PolesCount=3 KnotsCount=2 Degree=2 IsPeriodic=0
    g4: GeomPoint X=0 Y=0 Z=0
    g5: GeomPoint X=8 Y=6 Z=0
    g6: LineSegment StartX=0 StartY=6 StartZ=0 EndX=8 EndY=6 EndZ=0
  constraints (14):
    c: Coincident(g0,g-1)
    c: Distance(g0) = 6
    c: Vertical(g0)
    c: Coincident(g3,g0)
    c: Weight(g1) = 1
    c: Equal(g1,g2)
    c: InternalAlignment(g1,g3)
    c: InternalAlignment(g2,g3)
    c: InternalAlignment(g4,g3)
    c: InternalAlignment(g5,g3)
    c: Block(g3)
    c: Coincident(g6,g0)
    c: Coincident(g6,g3)
    c: Horizontal(g6)
FEATURE [Part::Extrusion] Extrude014  label="caseScrewPillarBracket002"
  Base = -> Sketch020
  Dir = (0,0,1)
  DirMode = 2
  FaceMakerClass = Part::FaceMakerBullseye
  LengthFwd = 2.4
  LengthRev = 0
  Placement = pos=(13.7,29,13.26) rot=(0,1,0;-1.5708rad)
  Solid = true
  Symmetric = false
FEATURE [Sketcher::SketchObject] Sketch021
  FullyConstrained = true
  sketch-geometry (7):
    g0: LineSegment StartX=0 StartY=0 StartZ=0 EndX=0 EndY=6 EndZ=0
    g1: Circle CenterX=0 CenterY=0 CenterZ=0 NormalX=0 NormalY=0 NormalZ=1 AngleXU=0 Radius=1
    g2: Circle CenterX=8 CenterY=6 CenterZ=0 NormalX=0 NormalY=0 NormalZ=1 AngleXU=0 Radius=1
    g3: BSplineCurve PolesCount=3 KnotsCount=2 Degree=2 IsPeriodic=0
    g4: GeomPoint X=0 Y=0 Z=0
    g5: GeomPoint X=8 Y=6 Z=0
    g6: LineSegment StartX=0 StartY=6 StartZ=0 EndX=8 EndY=6 EndZ=0
  constraints (14):
    c: Coincident(g0,g-1)
    c: Distance(g0) = 6
    c: Vertical(g0)
    c: Coincident(g3,g0)
    c: Weight(g1) = 1
    c: Equal(g1,g2)
    c: InternalAlignment(g1,g3)
    c: InternalAlignment(g2,g3)
    c: InternalAlignment(g4,g3)
    c: InternalAlignment(g5,g3)
    c: Block(g3)
    c: Coincident(g6,g0)
    c: Coincident(g6,g3)
    c: Horizontal(g6)
FEATURE [Part::Extrusion] Extrude015  label="caseScrewPillarBracket003"
  Base = -> Sketch021
  Dir = (0,0,1)
  DirMode = 2
  FaceMakerClass = Part::FaceMakerBullseye
  LengthFwd = 2.4
  LengthRev = 0
  Placement = pos=(11.3,29,58.74) rot=(0,1,0;1.5708rad)
  Solid = true
  Symmetric = false
FEATURE [Sketcher::SketchObject] Sketch022
  FullyConstrained = true
  sketch-geometry (7):
    g0: LineSegment StartX=0 StartY=0 StartZ=0 EndX=0 EndY=6 EndZ=0
    g1: Circle CenterX=0 CenterY=0 CenterZ=0 NormalX=0 NormalY=0 NormalZ=1 AngleXU=0 Radius=1
    g2: Circle CenterX=8 CenterY=6 CenterZ=0 NormalX=0 NormalY=0 NormalZ=1 AngleXU=0 Radius=1
    g3: BSplineCurve PolesCount=3 KnotsCount=2 Degree=2 IsPeriodic=0
    g4: GeomPoint X=0 Y=0 Z=0
    g5: GeomPoint X=8 Y=6 Z=0
    g6: LineSegment StartX=0 StartY=6 StartZ=0 EndX=8 EndY=6 EndZ=0
  constraints (14):
    c: Coincident(g0,g-1)
    c: Distance(g0) = 6
    c: Vertical(g0)
    c: Coincident(g3,g0)
    c: Weight(g1) = 1
    c: Equal(g1,g2)
    c: InternalAlignment(g1,g3)
    c: InternalAlignment(g2,g3)
    c: InternalAlignment(g4,g3)
    c: InternalAlignment(g5,g3)
    c: Block(g3)
    c: Coincident(g6,g0)
    c: Coincident(g6,g3)
    c: Horizontal(g6)
FEATURE [Part::Extrusion] Extrude016  label="caseScrewPillarBracket004"
  Base = -> Sketch022
  Dir = (0,0,1)
  DirMode = 2
  FaceMakerClass = Part::FaceMakerBullseye
  LengthFwd = 2.4
  LengthRev = 0
  Placement = pos=(88.3,29,65.23) rot=(0,1,0;1.5708rad)
  Solid = true
  Symmetric = false
FEATURE [Sketcher::SketchObject] Sketch023
  FullyConstrained = true
  sketch-geometry (7):
    g0: LineSegment StartX=0 StartY=0 StartZ=0 EndX=0 EndY=6 EndZ=0
    g1: Circle CenterX=0 CenterY=0 CenterZ=0 NormalX=0 NormalY=0 NormalZ=1 AngleXU=0 Radius=1
    g2: Circle CenterX=8 CenterY=6 CenterZ=0 NormalX=0 NormalY=0 NormalZ=1 AngleXU=0 Radius=1
    g3: BSplineCurve PolesCount=3 KnotsCount=2 Degree=2 IsPeriodic=0
    g4: GeomPoint X=0 Y=0 Z=0
    g5: GeomPoint X=8 Y=6 Z=0
    g6: LineSegment StartX=0 StartY=6 StartZ=0 EndX=8 EndY=6 EndZ=0
  constraints (14):
    c: Coincident(g0,g-1)
    c: Distance(g0) = 6
    c: Vertical(g0)
    c: Coincident(g3,g0)
    c: Weight(g1) = 1
    c: Equal(g1,g2)
    c: InternalAlignment(g1,g3)
    c: InternalAlignment(g2,g3)
    c: InternalAlignment(g4,g3)
    c: InternalAlignment(g5,g3)
    c: Block(g3)
    c: Coincident(g6,g0)
    c: Coincident(g6,g3)
    c: Horizontal(g6)
FEATURE [Part::Extrusion] Extrude017  label="caseScrewPillarBracket005"
  Base = -> Sketch023
  Dir = (0,0,1)
  DirMode = 2
  FaceMakerClass = Part::FaceMakerBullseye
  LengthFwd = 2.4
  LengthRev = 0
  Placement = pos=(90.7,29,6.77) rot=(0,-1,0;1.5708rad)
  Solid = true
  Symmetric = false
FEATURE [Sketcher::SketchObject] Sketch024
  FullyConstrained = true
  sketch-geometry (7):
    g0: LineSegment StartX=0 StartY=0 StartZ=0 EndX=0 EndY=6 EndZ=0
    g1: Circle CenterX=0 CenterY=0 CenterZ=0 NormalX=0 NormalY=0 NormalZ=1 AngleXU=0 Radius=1
    g2: Circle CenterX=8 CenterY=6 CenterZ=0 NormalX=0 NormalY=0 NormalZ=1 AngleXU=0 Radius=1
    g3: BSplineCurve PolesCount=3 KnotsCount=2 Degree=2 IsPeriodic=0
    g4: GeomPoint X=0 Y=0 Z=0
    g5: GeomPoint X=8 Y=6 Z=0
    g6: LineSegment StartX=0 StartY=6 StartZ=0 EndX=8 EndY=6 EndZ=0
  constraints (14):
    c: Coincident(g0,g-1)
    c: Distance(g0) = 6
    c: Vertical(g0)
    c: Coincident(g3,g0)
    c: Weight(g1) = 1
    c: Equal(g1,g2)
    c: InternalAlignment(g1,g3)
    c: InternalAlignment(g2,g3)
    c: InternalAlignment(g4,g3)
    c: InternalAlignment(g5,g3)
    c: Block(g3)
    c: Coincident(g6,g0)
    c: Coincident(g6,g3)
    c: Horizontal(g6)
FEATURE [Part::Extrusion] Extrude018  label="caseScrewPillarBracket006"
  Base = -> Sketch024
  Dir = (0,0,1)
  DirMode = 2
  FaceMakerClass = Part::FaceMakerBullseye
  LengthFwd = 2.4
  LengthRev = 0
  Placement = pos=(103.7,29,6.77) rot=(0,-1,0;1.5708rad)
  Solid = true
  Symmetric = false
FEATURE [Sketcher::SketchObject] Sketch025
  FullyConstrained = true
  sketch-geometry (7):
    g0: LineSegment StartX=0 StartY=0 StartZ=0 EndX=0 EndY=6 EndZ=0
    g1: Circle CenterX=0 CenterY=0 CenterZ=0 NormalX=0 NormalY=0 NormalZ=1 AngleXU=0 Radius=1
    g2: Circle CenterX=8 CenterY=6 CenterZ=0 NormalX=0 NormalY=0 NormalZ=1 AngleXU=0 Radius=1
    g3: BSplineCurve PolesCount=3 KnotsCount=2 Degree=2 IsPeriodic=0
    g4: GeomPoint X=0 Y=0 Z=0
    g5: GeomPoint X=8 Y=6 Z=0
    g6: LineSegment StartX=0 StartY=6 StartZ=0 EndX=8 EndY=6 EndZ=0
  constraints (14):
    c: Coincident(g0,g-1)
    c: Distance(g0) = 6
    c: Vertical(g0)
    c: Coincident(g3,g0)
    c: Weight(g1) = 1
    c: Equal(g1,g2)
    c: InternalAlignment(g1,g3)
    c: InternalAlignment(g2,g3)
    c: InternalAlignment(g4,g3)
    c: InternalAlignment(g5,g3)
    c: Block(g3)
    c: Coincident(g6,g0)
    c: Coincident(g6,g3)
    c: Horizontal(g6)
FEATURE [Part::Extrusion] Extrude019  label="caseScrewPillarBracket007"
  Base = -> Sketch025
  Dir = (0,0,1)
  DirMode = 2
  FaceMakerClass = Part::FaceMakerBullseye
  LengthFwd = 2.4
  LengthRev = 0
  Placement = pos=(101.3,29,65.23) rot=(0,1,0;1.5708rad)
  Solid = true
  Symmetric = false
FEATURE [Part::Box] Box011  label="frontCaseScrewPillarBracket"
  AttacherType = Attacher::AttachEngine3D
  Height = 2.4
  Length = 16
  Placement = pos=(87,28,2.3) rot=(0,0,1;0rad)
  Width = 7
FEATURE [Part::Box] Box012  label="frontCaseScrewPillarBracket001"
  AttacherType = Attacher::AttachEngine3D
  Height = 2.4
  Length = 16
  Placement = pos=(87,28,67.3) rot=(0,0,1;0rad)
  Width = 7
FEATURE [Sketcher::SketchObject] Sketch026
  FullyConstrained = true
  sketch-geometry (17):
    g0: Circle CenterX=-3.5 CenterY=23.5 CenterZ=0 NormalX=0 NormalY=0 NormalZ=1 AngleXU=0 Radius=1
    g1: Circle CenterX=-1 CenterY=15.25 CenterZ=0 NormalX=0 NormalY=0 NormalZ=1 AngleXU=0 Radius=1
    g2: Circle CenterX=-3.5 CenterY=7 CenterZ=0 NormalX=0 NormalY=0 NormalZ=1 AngleXU=0 Radius=1
    g3: BSplineCurve PolesCount=3 KnotsCount=2 Degree=2 IsPeriodic=0
    g4: GeomPoint X=-3.5 Y=23.5 Z=0
    g5: GeomPoint X=-3.5 Y=7 Z=0
    g6: Circle CenterX=-4.8 CenterY=30.5 CenterZ=0 NormalX=0 NormalY=0 NormalZ=1 AngleXU=0 Radius=1
    g7: Circle CenterX=-3.5 CenterY=30.5 CenterZ=0 NormalX=0 NormalY=0 NormalZ=1 AngleXU=0 Radius=1
    g8: Circle CenterX=-3.5 CenterY=29.2 CenterZ=0 NormalX=0 NormalY=0 NormalZ=1 AngleXU=0 Radius=1
    g9: BSplineCurve PolesCount=3 KnotsCount=2 Degree=2 IsPeriodic=0
    g10: GeomPoint X=-4.8 Y=30.5 Z=0
    g11: GeomPoint X=-3.5 Y=29.2 Z=0
    g12: LineSegment StartX=-3.5 StartY=29.2 StartZ=0 EndX=-3.5 EndY=23.5 EndZ=0
    g13: LineSegment StartX=-4.8 StartY=30.5 StartZ=0 EndX=0 EndY=30.5 EndZ=0
    g14: LineSegment StartX=-3.5 StartY=5 StartZ=0 EndX=-3.5 EndY=7 EndZ=0
    g15: LineSegment StartX=0 StartY=5 StartZ=0 EndX=0 EndY=30.5 EndZ=0
    g16: LineSegment StartX=-3.5 StartY=5 StartZ=0 EndX=0 EndY=5 EndZ=0
  constraints (33):
    c: Weight(g0) = 1
    c: Equal(g0,g1)
    c: Equal(g0,g2)
    c: InternalAlignment(g0,g3)
    c: InternalAlignment(g1,g3)
    c: InternalAlignment(g2,g3)
    c: InternalAlignment(g4,g3)
    c: InternalAlignment(g5,g3)
    c: Block(g3)
    c: Weight(g6) = 1
    c: Equal(g6,g7)
    c: Equal(g6,g8)
    c: InternalAlignment(g6,g9)
    c: InternalAlignment(g7,g9)
    c: InternalAlignment(g8,g9)
    c: InternalAlignment(g10,g9)
    c: InternalAlignment(g11,g9)
    c: Block(g9)
    c: Coincident(g12,g9)
    c: Coincident(g12,g3)
    c: Vertical(g12)
    c: Coincident(g13,g9)
    c: Horizontal(g13)
    c: Distance(g13) = 4.8
    c: Coincident(g14,g3)
    c: Vertical(g14)
    c: Coincident(g15,g13)
    c: Vertical(g15)
    c: Tangent(g15,g1)
    c: Distance(g14) = 2
    c: Coincident(g16,g14)
    c: Horizontal(g16)
    c: Coincident(g15,g16)
FEATURE [Part::Feature] Face050
  shape: bbox 4.8 x 25.5 x 2e-07 mm, 1 faces, 0 solids (baked)
FEATURE [Part::Revolution] Revolve054  label="moreFrontCaseScrewPost001"
  Angle = 360
  Axis = (0,1,0)
  Base = (0,0,0)
  FaceMakerClass = Part::FaceMakerBullseye
  Placement = pos=(102.5,4.5,3.5) rot=(0,0,1;0rad)
  Solid = false
  Source = -> Face050
  Symmetric = false
FEATURE [Part::Feature] Face051
  shape: bbox 4.8 x 25.5 x 2e-07 mm, 1 faces, 0 solids (baked)
FEATURE [Part::Revolution] Revolve055  label="moreFrontCaseScrewPost002"
  Angle = 360
  Axis = (0,1,0)
  Base = (0,0,0)
  FaceMakerClass = Part::FaceMakerBullseye
  Placement = pos=(102.5,4.5,68.5) rot=(0,0,1;0rad)
  Solid = false
  Source = -> Face051
  Symmetric = false
FEATURE [Sketcher::SketchObject] Sketch027
  FullyConstrained = true
  sketch-geometry (10):
    g0: LineSegment StartX=-1.6 StartY=4.7 StartZ=0 EndX=-1.6 EndY=1.7 EndZ=0
    g1: LineSegment StartX=-3.5 StartY=4.7 StartZ=0 EndX=-1.6 EndY=4.7 EndZ=0
    g2: LineSegment StartX=-1.6 StartY=1.7 StartZ=0 EndX=-1.6 EndY=1.5 EndZ=0
    g3: LineSegment StartX=-1.6 StartY=1.5 StartZ=0 EndX=-5.2 EndY=1.5 EndZ=0
    g4: Circle CenterX=-3.5 CenterY=4.7 CenterZ=0 NormalX=0 NormalY=0 NormalZ=1 AngleXU=0 Radius=1
    g5: Circle CenterX=-3.59627 CenterY=2.99743 CenterZ=0 NormalX=0 NormalY=0 NormalZ=1 AngleXU=0 Radius=1
    g6: Circle CenterX=-5.2 CenterY=1.5 CenterZ=0 NormalX=0 NormalY=0 NormalZ=1 AngleXU=0 Radius=1
    g7: BSplineCurve PolesCount=3 KnotsCount=2 Degree=2 IsPeriodic=0
    g8: GeomPoint X=-3.5 Y=4.7 Z=0
    g9: GeomPoint X=-5.2 Y=1.5 Z=0
  constraints (23):
    c: Vertical(g0)
    c: Distance(g0) = 3
    c: Coincident(g1,g0)
    c: Horizontal(g1)
    c: Block(g0)
    c: Block(g1)
    c: Coincident(g2,g0)
    c: Vertical(g2)
    c: Distance(g2) = 0.2
    c: Coincident(g3,g2)
    c: Horizontal(g3)
    c: Block(g3)
    c: Coincident(g7,g1)
    c: Weight(g4) = 1
    c: Equal(g4,g5)
    c: Equal(g4,g6)
    c: Coincident(g7,g3)
    c: InternalAlignment(g4,g7)
    c: InternalAlignment(g5,g7)
    c: InternalAlignment(g6,g7)
    c: InternalAlignment(g8,g7)
    c: InternalAlignment(g9,g7)
    c: Block(g7)
FEATURE [Sketcher::SketchObject] Sketch028
  FullyConstrained = true
  sketch-geometry (18):
    g0: LineSegment StartX=0 StartY=3e-16 StartZ=0 EndX=0 EndY=1.7 EndZ=0
    g1: LineSegment StartX=-3.5 StartY=0 StartZ=0 EndX=-3.5 EndY=0.9 EndZ=0
    g2: Circle CenterX=-2.7 CenterY=1.7 CenterZ=0 NormalX=0 NormalY=0 NormalZ=1 AngleXU=0 Radius=1
    g3: Circle CenterX=-3.5 CenterY=1.7 CenterZ=0 NormalX=0 NormalY=0 NormalZ=1 AngleXU=0 Radius=1
    g4: Circle CenterX=-3.5 CenterY=0.9 CenterZ=0 NormalX=0 NormalY=0 NormalZ=1 AngleXU=0 Radius=1
    g5: BSplineCurve PolesCount=3 KnotsCount=2 Degree=2 IsPeriodic=0
    g6: GeomPoint X=-2.7 Y=1.7 Z=0
    g7: GeomPoint X=-3.5 Y=0.9 Z=0
    g8: LineSegment StartX=-3.5 StartY=0 StartZ=0 EndX=-3.5 EndY=-7 EndZ=0
    g9: LineSegment StartX=0 StartY=3e-16 StartZ=0 EndX=0 EndY=-7 EndZ=0
    g10: LineSegment StartX=-3.5 StartY=-7 StartZ=0 EndX=0 EndY=-7 EndZ=0
    g11: LineSegment StartX=-2.7 StartY=1.7 StartZ=0 EndX=-1.6 EndY=1.7 EndZ=0
    g12: LineSegment StartX=0 StartY=1.7 StartZ=0 EndX=0 EndY=4.5 EndZ=0
    g13: LineSegment StartX=0 StartY=4.5 StartZ=0 EndX=0 EndY=10.8 EndZ=0
    g14: LineSegment StartX=0 StartY=10.8 StartZ=0 EndX=-2 EndY=10.8 EndZ=0
    g15: LineSegment StartX=-1.6 StartY=4.7 StartZ=0 EndX=-1.6 EndY=1.7 EndZ=0
    g16: LineSegment StartX=-1.6 StartY=4.7 StartZ=0 EndX=-2 EndY=4.7 EndZ=0
    g17: LineSegment StartX=-2 StartY=4.7 StartZ=0 EndX=-2 EndY=10.8 EndZ=0
  constraints (44):
    c: Vertical(g0)
    c: Vertical(g1)
    c: Distance(g1) = 0.9
    c: Block(g0)
    c: Distance(g0) = 1.7
    c: Weight(g2) = 1
    c: Equal(g2,g3)
    c: Equal(g2,g4)
    c: Coincident(g5,g1)
    c: InternalAlignment(g2,g5)
    c: InternalAlignment(g3,g5)
    c: InternalAlignment(g4,g5)
    c: InternalAlignment(g6,g5)
    c: InternalAlignment(g7,g5)
    c: Block(g5)
    c: Coincident(g8,g1)
    c: Vertical(g8)
    c: Distance(g8) = 7
    c: Vertical(g9)
    c: Equal(g8,g9) = 7
    c: Coincident(g9,g0)
    c: Coincident(g10,g8)
    c: Coincident(g10,g9)
    c: Horizontal(g10)
    c: Coincident(g11,g5)
    c: Horizontal(g11)
    c: Coincident(g12,g0)
    c: Vertical(g12)
    c: Distance(g12) = 2.8
    c: Coincident(g13,g12)
    c: Vertical(g13)
    c: Distance(g13) = 6.3
    c: Coincident(g14,g13)
    c: Horizontal(g14)
    c: Distance(g14) = 2
    c: Vertical(g15)
    c: Distance(g15) = 3
    c: Block(g11)
    c: Coincident(g15,g11)
    c: Coincident(g16,g15)
    c: Horizontal(g16)
    c: Coincident(g17,g16)
    c: Coincident(g17,g14)
    c: Vertical(g17)
FEATURE [Part::Revolution] Revolve040  label="backCaseScrewRetainer001"
  Angle = 360
  Axis = (0,1,0)
  Base = (0,0,0)
  FaceMakerClass = Part::FaceMakerBullseye
  Placement = pos=(12.5,3,10) rot=(0,0,1;0rad)
  Solid = false
  Source = -> Face036
  Symmetric = false
FEATURE [Part::Feature] Face055
  shape: bbox 3.5 x 30.2 x 2e-07 mm, 1 faces, 0 solids (baked)
FEATURE [Part::Revolution] Revolve059  label="backCaseScrewPost"
  Angle = 360
  Axis = (0,1,0)
  Base = (0,0,0)
  FaceMakerClass = Part::FaceMakerBullseye
  Placement = pos=(12.5,4.5,10) rot=(0,0,1;0rad)
  Solid = false
  Source = -> Face055
  Symmetric = false
FEATURE [Part::Feature] Face056
  shape: bbox 3.5 x 30.2 x 2e-07 mm, 1 faces, 0 solids (baked)
FEATURE [Part::Revolution] Revolve060  label="backCaseScrewPost001"
  Angle = 360
  Axis = (0,1,0)
  Base = (0,0,0)
  FaceMakerClass = Part::FaceMakerBullseye
  Placement = pos=(12.5,4.5,62) rot=(0,0,1;0rad)
  Solid = false
  Source = -> Face056
  Symmetric = false
FEATURE [Part::Feature] Face057
  shape: bbox 3.5 x 17.8 x 2e-07 mm, 1 faces, 0 solids (baked)
FEATURE [Part::Revolution] Revolve061  label="removeToCreateScrewAndThreadedInsertHole"
  Angle = 360
  Axis = (0,1,0)
  Base = (0,0,0)
  FaceMakerClass = Part::FaceMakerBullseye
  Placement = pos=(12.5,0,10) rot=(0,0,1;0rad)
  Solid = false
  Source = -> Face057
  Symmetric = false
FEATURE [Part::Feature] Face058
  shape: bbox 3.5 x 17.8 x 2e-07 mm, 1 faces, 0 solids (baked)
FEATURE [Part::Revolution] Revolve062  label="removeToCreateScrewAndThreadedInsertHole001"
  Angle = 360
  Axis = (0,1,0)
  Base = (0,0,0)
  FaceMakerClass = Part::FaceMakerBullseye
  Placement = pos=(12.5,0,62) rot=(0,0,1;0rad)
  Solid = false
  Source = -> Face058
  Symmetric = false
FEATURE [Part::Feature] Face059
  shape: bbox 3.5 x 17.8 x 2e-07 mm, 1 faces, 0 solids (baked)
FEATURE [Part::Revolution] Revolve063  label="removeToCreateScrewAndThreadedInsertHole002"
  Angle = 360
  Axis = (0,1,0)
  Base = (0,0,0)
  FaceMakerClass = Part::FaceMakerBullseye
  Placement = pos=(89.5,0,68.5) rot=(0,0,1;0rad)
  Solid = false
  Source = -> Face059
  Symmetric = false
FEATURE [Part::Feature] Face060
  shape: bbox 3.5 x 17.8 x 2e-07 mm, 1 faces, 0 solids (baked)
FEATURE [Part::Revolution] Revolve064  label="removeToCreateScrewAndThreadedInsertHole003"
  Angle = 360
  Axis = (0,1,0)
  Base = (0,0,0)
  FaceMakerClass = Part::FaceMakerBullseye
  Placement = pos=(89.5,0,3.5) rot=(0,0,1;0rad)
  Solid = false
  Source = -> Face060
  Symmetric = false
FEATURE [Part::Feature] Face061
  shape: bbox 3.5 x 17.8 x 2e-07 mm, 1 faces, 0 solids (baked)
FEATURE [Part::Revolution] Revolve065  label="removeToCreateScrewAndThreadedInsertHole004"
  Angle = 360
  Axis = (0,1,0)
  Base = (0,0,0)
  FaceMakerClass = Part::FaceMakerBullseye
  Placement = pos=(102.5,4.7,3.5) rot=(0,0,1;0rad)
  Solid = false
  Source = -> Face061
  Symmetric = false
FEATURE [Part::Feature] Face062
  shape: bbox 3.5 x 17.8 x 2e-07 mm, 1 faces, 0 solids (baked)
FEATURE [Part::Revolution] Revolve066  label="removeToCreateScrewAndThreadedInsertHole005"
  Angle = 360
  Axis = (0,1,0)
  Base = (0,0,0)
  FaceMakerClass = Part::FaceMakerBullseye
  Placement = pos=(102.5,4.7,68.5) rot=(0,0,1;0rad)
  Solid = false
  Source = -> Face062
  Symmetric = false
FEATURE [Part::MultiFuse] Fusion047  label="makeHoles"
  Shapes = -> [Revolve066,Revolve065,Revolve064,Revolve063,Revolve062,Revolve061]
FEATURE [Part::Feature] Face063
  shape: bbox 3.6 x 3.2 x 2e-07 mm, 1 faces, 0 solids (baked)
FEATURE [Part::Revolution] Revolve067  label="moreFrontCaseScrewRetainer002"
  Angle = 360
  Axis = (0,1,0)
  Base = (0,0,0)
  FaceMakerClass = Part::FaceMakerBullseye
  Placement = pos=(102.5,4.5,68.5) rot=(0,0,1;0rad)
  Solid = false
  Source = -> Face063
  Symmetric = false
FEATURE [Part::Feature] Face064
  shape: bbox 3.6 x 3.2 x 2e-07 mm, 1 faces, 0 solids (baked)
FEATURE [Part::Revolution] Revolve068  label="moreFrontCaseScrewRetainer003"
  Angle = 360
  Axis = (0,1,0)
  Base = (0,0,0)
  FaceMakerClass = Part::FaceMakerBullseye
  Placement = pos=(102.5,4.5,3.5) rot=(0,0,1;0rad)
  Solid = false
  Source = -> Face064
  Symmetric = false
FEATURE [Part::Feature] Face065
  shape: bbox 3.5 x 17.8 x 2e-07 mm, 1 faces, 0 solids (baked)
FEATURE [Part::Revolution] Revolve069  label="removeToCreateScrewAndThreadedInsertHole006"
  Angle = 360
  Axis = (0,1,0)
  Base = (0,0,0)
  FaceMakerClass = Part::FaceMakerBullseye
  Placement = pos=(12.5,0,10) rot=(0,0,1;0rad)
  Solid = false
  Source = -> Face065
  Symmetric = false
FEATURE [Part::Feature] Face066
  shape: bbox 3.5 x 17.8 x 2e-07 mm, 1 faces, 0 solids (baked)
FEATURE [Part::Revolution] Revolve070  label="removeToCreateScrewAndThreadedInsertHole007"
  Angle = 360
  Axis = (0,1,0)
  Base = (0,0,0)
  FaceMakerClass = Part::FaceMakerBullseye
  Placement = pos=(12.5,0,62) rot=(0,0,1;0rad)
  Solid = false
  Source = -> Face066
  Symmetric = false
FEATURE [Part::Feature] Face067
  shape: bbox 3.5 x 17.8 x 2e-07 mm, 1 faces, 0 solids (baked)
FEATURE [Part::Revolution] Revolve071  label="removeToCreateScrewAndThreadedInsertHole008"
  Angle = 360
  Axis = (0,1,0)
  Base = (0,0,0)
  FaceMakerClass = Part::FaceMakerBullseye
  Placement = pos=(89.5,0,68.5) rot=(0,0,1;0rad)
  Solid = false
  Source = -> Face067
  Symmetric = false
FEATURE [Part::Feature] Face068
  shape: bbox 3.5 x 17.8 x 2e-07 mm, 1 faces, 0 solids (baked)
FEATURE [Part::Revolution] Revolve072  label="removeToCreateScrewAndThreadedInsertHole009"
  Angle = 360
  Axis = (0,1,0)
  Base = (0,0,0)
  FaceMakerClass = Part::FaceMakerBullseye
  Placement = pos=(89.5,0,3.5) rot=(0,0,1;0rad)
  Solid = false
  Source = -> Face068
  Symmetric = false
FEATURE [Part::Feature] Face069
  shape: bbox 3.5 x 17.8 x 2e-07 mm, 1 faces, 0 solids (baked)
FEATURE [Part::Feature] Face070
  shape: bbox 3.5 x 17.8 x 2e-07 mm, 1 faces, 0 solids (baked)
FEATURE [Part::Revolution] Revolve073  label="removeToCreateScrewAndThreadedInsertHole010"
  Angle = 360
  Axis = (0,1,0)
  Base = (0,0,0)
  FaceMakerClass = Part::FaceMakerBullseye
  Placement = pos=(102.5,4.7,3.5) rot=(0,0,1;0rad)
  Solid = false
  Source = -> Face069
  Symmetric = false
FEATURE [Part::Revolution] Revolve074  label="removeToCreateScrewAndThreadedInsertHole011"
  Angle = 360
  Axis = (0,1,0)
  Base = (0,0,0)
  FaceMakerClass = Part::FaceMakerBullseye
  Placement = pos=(102.5,4.7,68.5) rot=(0,0,1;0rad)
  Solid = false
  Source = -> Face070
  Symmetric = false
FEATURE [Part::MultiFuse] Fusion048  label="makeHoles001"
  Shapes = -> [Revolve074,Revolve073,Revolve072,Revolve071,Revolve070,Revolve069]
FEATURE [Part::MultiFuse] Fusion049  label="caseScrewRetainers"
  Shapes = -> [Revolve067,Revolve068,Revolve048,Revolve047,Revolve039,Revolve040]
FEATURE [Part::Cut] Cut015  label="caseScrewRetainers001"
  Base = -> Fusion049
  Tool = -> Fusion048
FEATURE [Part::MultiFuse] Fusion050  label="casePillars"
  Shapes = -> [Revolve055,Revolve054,Revolve043,Revolve046,Revolve059,Revolve060]
FEATURE [Part::Feature] Face071 .. Face076  x6 (patterned run collapsed; names and placements below)
  shape: bbox 3.5 x 17.8 x 2e-07 mm, 1 faces, 0 solids (baked)
FEATURE [Part::Revolution] Revolve075  label="removeToCreateScrewAndThreadedInsertHole012"
  Angle = 360
  Axis = (0,1,0)
  Base = (0,0,0)
  FaceMakerClass = Part::FaceMakerBullseye
  Placement = pos=(12.5,0,10) rot=(0,0,1;0rad)
  Solid = false
  Source = -> Face071
  Symmetric = false
FEATURE [Part::Revolution] Revolve076  label="removeToCreateScrewAndThreadedInsertHole013"
  Angle = 360
  Axis = (0,1,0)
  Base = (0,0,0)
  FaceMakerClass = Part::FaceMakerBullseye
  Placement = pos=(12.5,0,62) rot=(0,0,1;0rad)
  Solid = false
  Source = -> Face072
  Symmetric = false
FEATURE [Part::Revolution] Revolve077  label="removeToCreateScrewAndThreadedInsertHole014"
  Angle = 360
  Axis = (0,1,0)
  Base = (0,0,0)
  FaceMakerClass = Part::FaceMakerBullseye
  Placement = pos=(89.5,0,68.5) rot=(0,0,1;0rad)
  Solid = false
  Source = -> Face073
  Symmetric = false
FEATURE [Part::Revolution] Revolve078  label="removeToCreateScrewAndThreadedInsertHole015"
  Angle = 360
  Axis = (0,1,0)
  Base = (0,0,0)
  FaceMakerClass = Part::FaceMakerBullseye
  Placement = pos=(89.5,0,3.5) rot=(0,0,1;0rad)
  Solid = false
  Source = -> Face074
  Symmetric = false
FEATURE [Part::Revolution] Revolve079  label="removeToCreateScrewAndThreadedInsertHole016"
  Angle = 360
  Axis = (0,1,0)
  Base = (0,0,0)
  FaceMakerClass = Part::FaceMakerBullseye
  Placement = pos=(102.5,4.7,3.5) rot=(0,0,1;0rad)
  Solid = false
  Source = -> Face075
  Symmetric = false
FEATURE [Part::Revolution] Revolve080  label="removeToCreateScrewAndThreadedInsertHole017"
  Angle = 360
  Axis = (0,1,0)
  Base = (0,0,0)
  FaceMakerClass = Part::FaceMakerBullseye
  Placement = pos=(102.5,4.7,68.5) rot=(0,0,1;0rad)
  Solid = false
  Source = -> Face076
  Symmetric = false
FEATURE [Part::MultiFuse] Fusion051  label="makeHoles002"
  Shapes = -> [Revolve080,Revolve079,Revolve078,Revolve077,Revolve076,Revolve075]
FEATURE [Part::Cut] Cut016  label="caesPillars"
  Base = -> Fusion050
  Tool = -> Fusion051
FEATURE [Part::Revolution] Revolve009  label="plugHousing016"
  Angle = 360
  Axis = (0,1,0)
  Base = (0,0,0)
  FaceMakerClass = Part::FaceMakerBullseye
  Placement = pos=(0,0,36.15) rot=(0,0,1;0rad)
  Solid = false
  Source = -> Face012
  Symmetric = false
FEATURE [Part::MultiFuse] Fusion014  label="plugHousing023"
  Placement = pos=(0,0,0) rot=(0,0,1;1.5708rad)
  Shapes = -> [Revolve011,Revolve009]
FEATURE [Part::Revolution] Revolve010  label="plugHousing017"
  Angle = 360
  Axis = (0,1,0)
  Base = (0,0,0)
  FaceMakerClass = Part::FaceMakerBullseye
  Placement = pos=(0,0,36.15) rot=(0,0,1;0rad)
  Solid = false
  Source = -> Face014
  Symmetric = false
FEATURE [Part::MultiFuse] Fusion015  label="plugHousing024"
  Placement = pos=(0,0,0) rot=(0,0,1;1.5708rad)
  Shapes = -> [Revolve010,Revolve015]
FEATURE [Part::Revolution] Revolve014  label="plugHousing026"
  Angle = 360
  Axis = (0,1,0)
  Base = (0,0,0)
  FaceMakerClass = Part::FaceMakerBullseye
  Placement = pos=(0,0,36.15) rot=(0,0,1;0rad)
  Solid = false
  Source = -> Face011
  Symmetric = false
FEATURE [Part::Revolution] Revolve013  label="plugHousing025"
  Angle = 360
  Axis = (0,1,0)
  Base = (0,0,0)
  FaceMakerClass = Part::FaceMakerBullseye
  Placement = pos=(0,0,36.15) rot=(0,0,1;0rad)
  Solid = false
  Source = -> Face015
  Symmetric = false
FEATURE [Part::MultiFuse] Fusion016  label="plugHousing028"
  Placement = pos=(0,19,0) rot=(0,0,1;3.14159rad)
  Shapes = -> [Fusion014,Fusion013]
FEATURE [Part::MultiFuse] Fusion011  label="plugHousing018"
  Placement = pos=(0,0,0) rot=(0,0,1;1.5708rad)
  Shapes = -> [Revolve014,Revolve013]
FEATURE [Part::MultiFuse] Fusion012  label="plugHousing019"
  Placement = pos=(0,19,0) rot=(0,0,1;3.14159rad)
  Shapes = -> [Fusion011,Fusion015]
FEATURE [Part::MultiFuse] Fusion017  label="plugHousing029"
  Placement = pos=(122.621,0,-0.15) rot=(0,0,1;0rad)
  Shapes = -> [Fusion016,Fusion012]
FEATURE [Part::MultiFuse] Fusion052  label="casePillarRetainers"
  Shapes = -> [Extrude012,Extrude013,Extrude014,Extrude015,Extrude016,Extrude017,Extrude018,Extrude019,Box011,Box012]
FEATURE [Part::Feature] Face077
  shape: bbox 3.5 x 17.8 x 2e-07 mm, 1 faces, 0 solids (baked)
FEATURE [Part::Revolution] Revolve081  label="removeToCreateScrewAndThreadedInsertHole018"
  Angle = 360
  Axis = (0,1,0)
  Base = (0,0,0)
  FaceMakerClass = Part::FaceMakerBullseye
  Placement = pos=(62.3,30.3,19.7) rot=(0,0,1;0rad)
  Solid = false
  Source = -> Face077
  Symmetric = false
FEATURE [Part::Feature] Face078
  shape: bbox 3.5 x 17.8 x 2e-07 mm, 1 faces, 0 solids (baked)
FEATURE [Part::Revolution] Revolve082  label="removeToCreateScrewAndThreadedInsertHole019"
  Angle = 360
  Axis = (0,1,0)
  Base = (0,0,0)
  FaceMakerClass = Part::FaceMakerBullseye
  Placement = pos=(62.3,30.3,51.7) rot=(0,0,1;0rad)
  Solid = false
  Source = -> Face078
  Symmetric = false
FEATURE [Part::Feature] Face079
  shape: bbox 3.5 x 17.8 x 2e-07 mm, 1 faces, 0 solids (baked)
FEATURE [Part::Revolution] Revolve083  label="removeToCreateScrewAndThreadedInsertHole020"
  Angle = 360
  Axis = (0,1,0)
  Base = (0,0,0)
  FaceMakerClass = Part::FaceMakerBullseye
  Placement = pos=(30.3,30.3,19.7) rot=(0,0,1;0rad)
  Solid = false
  Source = -> Face079
  Symmetric = false
FEATURE [Part::Feature] Face080
  shape: bbox 3.5 x 17.8 x 2e-07 mm, 1 faces, 0 solids (baked)
FEATURE [Part::Revolution] Revolve084  label="removeToCreateScrewAndThreadedInsertHole021"
  Angle = 360
  Axis = (0,1,0)
  Base = (0,0,0)
  FaceMakerClass = Part::FaceMakerBullseye
  Placement = pos=(30.3,30.3,51.7) rot=(0,0,1;0rad)
  Solid = false
  Source = -> Face080
  Symmetric = false
FEATURE [Part::MultiFuse] Fusion053  label="createThreadedInsertHolesForFan"
  Shapes = -> [Revolve081,Revolve082,Revolve083,Revolve084]
FEATURE [Part::Cut] Cut017  label="fanScrewHousing001"
  Base = -> Fusion046
  Tool = -> Fusion053
FEATURE [Part::Feature] Face081
  shape: bbox 3.5 x 17.8 x 2e-07 mm, 1 faces, 0 solids (baked)
FEATURE [Part::Revolution] Revolve085  label="removeToCreateScrewAndThreadedInsertHole022"
  Angle = 360
  Axis = (0,1,0)
  Base = (0,0,0)
  FaceMakerClass = Part::FaceMakerBullseye
  Placement = pos=(62.3,30.3,19.7) rot=(0,0,1;0rad)
  Solid = false
  Source = -> Face081
  Symmetric = false
FEATURE [Part::Feature] Face082
  shape: bbox 3.5 x 17.8 x 2e-07 mm, 1 faces, 0 solids (baked)
FEATURE [Part::Revolution] Revolve086  label="removeToCreateScrewAndThreadedInsertHole023"
  Angle = 360
  Axis = (0,1,0)
  Base = (0,0,0)
  FaceMakerClass = Part::FaceMakerBullseye
  Placement = pos=(62.3,30.3,51.7) rot=(0,0,1;0rad)
  Solid = false
  Source = -> Face082
  Symmetric = false
FEATURE [Part::Feature] Face083
  shape: bbox 3.5 x 17.8 x 2e-07 mm, 1 faces, 0 solids (baked)
FEATURE [Part::Revolution] Revolve087  label="removeToCreateScrewAndThreadedInsertHole024"
  Angle = 360
  Axis = (0,1,0)
  Base = (0,0,0)
  FaceMakerClass = Part::FaceMakerBullseye
  Placement = pos=(30.3,30.3,19.7) rot=(0,0,1;0rad)
  Solid = false
  Source = -> Face083
  Symmetric = false
FEATURE [Part::Feature] Face084
  shape: bbox 3.5 x 17.8 x 2e-07 mm, 1 faces, 0 solids (baked)
FEATURE [Part::Revolution] Revolve088  label="removeToCreateScrewAndThreadedInsertHole025"
  Angle = 360
  Axis = (0,1,0)
  Base = (0,0,0)
  FaceMakerClass = Part::FaceMakerBullseye
  Placement = pos=(30.3,30.3,51.7) rot=(0,0,1;0rad)
  Solid = false
  Source = -> Face084
  Symmetric = false
FEATURE [Part::MultiFuse] Fusion054  label="createThreadedInsertHolesForFan001"
  Shapes = -> [Revolve085,Revolve086,Revolve087,Revolve088]
FEATURE [Part::Cut] Cut018  label="top007"
  Base = -> Fusion040
  Tool = -> Fusion054
FEATURE [Sketcher::SketchObject] Sketch029
  FullyConstrained = false
  Placement = pos=(0,0,0) rot=(1,0,0;1.5708rad)
  sketch-geometry (24):
    g0: ArcOfCircle CenterX=-4 CenterY=-10.5 CenterZ=0 NormalX=0 NormalY=0 NormalZ=1 AngleXU=0 Radius=1.5 StartAngle=6e-16 EndAngle=3.14159
    g1: ArcOfCircle CenterX=-34.2 CenterY=-10.5 CenterZ=0 NormalX=0 NormalY=0 NormalZ=1 AngleXU=0 Radius=1.5 StartAngle=0 EndAngle=3.14159
    g2: ArcOfCircle CenterX=-34.2 CenterY=-27.7 CenterZ=0 NormalX=0 NormalY=0 NormalZ=1 AngleXU=0 Radius=1.5 StartAngle=3.14159 EndAngle=6.28319
    g3: ArcOfCircle CenterX=-4 CenterY=-27.7 CenterZ=0 NormalX=0 NormalY=0 NormalZ=1 AngleXU=0 Radius=1.5 StartAngle=3.1416 EndAngle=6.28319
    g4: ArcOfCircle CenterX=-10 CenterY=-4.3 CenterZ=0 NormalX=0 NormalY=0 NormalZ=1 AngleXU=0 Radius=1.5 StartAngle=2e-16 EndAngle=3.14159
    g5: ArcOfCircle CenterX=-16.1 CenterY=-1.8 CenterZ=0 NormalX=0 NormalY=0 NormalZ=1 AngleXU=0 Radius=1.5 StartAngle=5e-16 EndAngle=3.14159
    g6: ArcOfCircle CenterX=-22.1 CenterY=-1.8 CenterZ=0 NormalX=0 NormalY=0 NormalZ=1 AngleXU=0 Radius=1.5 StartAngle=5e-16 EndAngle=3.14159
    g7: ArcOfCircle CenterX=-28.2 CenterY=-4.3 CenterZ=0 NormalX=0 NormalY=0 NormalZ=1 AngleXU=0 Radius=1.5 StartAngle=2e-16 EndAngle=3.14159
    g8: ArcOfCircle CenterX=-10 CenterY=-33.9 CenterZ=0 NormalX=0 NormalY=0 NormalZ=1 AngleXU=0 Radius=1.5 StartAngle=3.14159 EndAngle=6.28319
    g9: ArcOfCircle CenterX=-16.1 CenterY=-36.4 CenterZ=0 NormalX=0 NormalY=0 NormalZ=1 AngleXU=0 Radius=1.5 StartAngle=3.14159 EndAngle=6.28319
    g10: ArcOfCircle CenterX=-22.1 CenterY=-36.4 CenterZ=0 NormalX=0 NormalY=0 NormalZ=1 AngleXU=0 Radius=1.5 StartAngle=3.14159 EndAngle=6.28319
    g11: ArcOfCircle CenterX=-28.2 CenterY=-33.9 CenterZ=0 NormalX=0 NormalY=0 NormalZ=1 AngleXU=0 Radius=1.5 StartAngle=3.14159 EndAngle=6.28319
    g12: LineSegment StartX=-35.7 StartY=-10.5 StartZ=0 EndX=-35.7 EndY=-27.7 EndZ=0
    g13: LineSegment StartX=-32.7 StartY=-10.5 StartZ=0 EndX=-32.7 EndY=-27.7 EndZ=0
    g14: LineSegment StartX=-29.7 StartY=-33.9 StartZ=0 EndX=-29.7 EndY=-4.3 EndZ=0
    g15: LineSegment StartX=-26.7 StartY=-33.9 StartZ=0 EndX=-26.7 EndY=-4.3 EndZ=0
    g16: LineSegment StartX=-2.5 StartY=-10.5 StartZ=0 EndX=-2.5 EndY=-27.7 EndZ=0
    g17: LineSegment StartX=-8.5 StartY=-4.3 StartZ=0 EndX=-8.5 EndY=-33.9 EndZ=0
    g18: LineSegment StartX=-5.5 StartY=-10.5 StartZ=0 EndX=-5.5 EndY=-27.7 EndZ=0
    g19: LineSegment StartX=-11.5 StartY=-4.3 StartZ=0 EndX=-11.5 EndY=-33.9 EndZ=0
    g20: LineSegment StartX=-14.6 StartY=-1.8 StartZ=0 EndX=-14.6 EndY=-36.4 EndZ=0
    g21: LineSegment StartX=-17.6 StartY=-1.8 StartZ=0 EndX=-17.6 EndY=-36.4 EndZ=0
    g22: LineSegment StartX=-20.6 StartY=-36.4 StartZ=0 EndX=-20.6 EndY=-1.8 EndZ=0
    g23: LineSegment StartX=-23.6 StartY=-1.8 StartZ=0 EndX=-23.6 EndY=-36.4 EndZ=0
  constraints (48):
    c: Block(g0)
    c: Block(g1)
    c: Block(g2)
    c: Block(g3)
    c: Block(g4)
    c: Block(g5)
    c: Block(g6)
    c: Block(g7)
    c: Block(g8)
    c: Block(g9)
    c: Block(g10)
    c: Block(g11)
    c: Coincident(g12,g1)
    c: Coincident(g12,g2)
    c: Vertical(g12)
    c: Coincident(g13,g1)
    c: Coincident(g13,g2)
    c: Vertical(g13)
    c: Coincident(g14,g11)
    c: Coincident(g14,g7)
    c: Vertical(g14)
    c: Coincident(g15,g11)
    c: Coincident(g15,g7)
    c: Vertical(g15)
    c: Coincident(g16,g0)
    c: Coincident(g16,g3)
    c: Vertical(g16)
    c: Coincident(g17,g4)
    c: Coincident(g17,g8)
    c: Vertical(g17)
    c: Coincident(g18,g0)
    c: Coincident(g18,g3)
    c: Vertical(g18)
    c: Coincident(g19,g4)
    c: Coincident(g19,g8)
    c: Vertical(g19)
    c: Coincident(g20,g5)
    c: Coincident(g20,g9)
    c: Vertical(g20)
    c: Coincident(g21,g5)
    c: Coincident(g21,g9)
    c: Vertical(g21)
    c: Coincident(g22,g10)
    c: Coincident(g22,g6)
    c: Vertical(g22)
    c: Coincident(g23,g6)
    c: Coincident(g23,g10)
    c: Vertical(g23)
FEATURE [Part::Extrusion] Extrude020  label="removeToCreateFanGrillHoles"
  Base = -> Sketch029
  Dir = (0,-1,6e-16)
  DirMode = 2
  FaceMakerClass = Part::FaceMakerBullseye
  LengthFwd = 10
  LengthRev = 0
  Placement = pos=(65.4,44,54.82) rot=(0,0,1;0rad)
  Solid = true
  Symmetric = false
FEATURE [Part::MultiFuse] Fusion055  label="top008"
  Shapes = -> [Cut017,Cut018]
FEATURE [Part::Cut] Cut019  label="top009"
  Base = -> Fusion055
  Tool = -> Extrude020
FEATURE [App::MeasureDistance] Distance003  label="Distance: 71.95 mm"
  Distance = 71.9513
  P1 = (117,38,72)
  P2 = (117,38,0.0487319)
FEATURE [Sketcher::SketchObject] Sketch030
  FullyConstrained = true
  Placement = pos=(117,19,0) rot=(0.57735,0.57735,0.57735;2.0944rad)
  sketch-geometry (48):
    g0: LineSegment StartX=-49.19 StartY=69.25 StartZ=0 EndX=-49.19 EndY=66.25 EndZ=0
    g1: LineSegment StartX=-49.19 StartY=63.5 StartZ=0 EndX=-49.19 EndY=60.5 EndZ=0
    g2: LineSegment StartX=-49.19 StartY=57.75 StartZ=0 EndX=-49.19 EndY=54.75 EndZ=0
    g3: LineSegment StartX=-49.19 StartY=52 StartZ=0 EndX=-49.19 EndY=49 EndZ=0
    g4: LineSegment StartX=-49.19 StartY=46.25 StartZ=0 EndX=-49.19 EndY=43.25 EndZ=0
    g5: LineSegment StartX=-49.19 StartY=40.5 StartZ=0 EndX=-49.19 EndY=37.5 EndZ=0
    g6: LineSegment StartX=-49.19 StartY=34.5 StartZ=0 EndX=-49.19 EndY=31.5 EndZ=0
    g7: LineSegment StartX=-49.19 StartY=28.75 StartZ=0 EndX=-49.19 EndY=25.75 EndZ=0
    g8: LineSegment StartX=-49.19 StartY=23 StartZ=0 EndX=-49.19 EndY=20 EndZ=0
    g9: LineSegment StartX=-49.19 StartY=17.25 StartZ=0 EndX=-49.19 EndY=14.25 EndZ=0
    g10: LineSegment StartX=-49.19 StartY=11.5 StartZ=0 EndX=-49.19 EndY=8.5 EndZ=0
    g11: LineSegment StartX=-49.19 StartY=5.75 StartZ=0 EndX=-49.19 EndY=2.75 EndZ=0
    g12: ArcOfCircle CenterX=-1.5 CenterY=67.75 CenterZ=0 NormalX=0 NormalY=0 NormalZ=1 AngleXU=0 Radius=1.5 StartAngle=4.71239 EndAngle=7.85398
    g13: ArcOfCircle CenterX=-1.5 CenterY=62 CenterZ=0 NormalX=0 NormalY=0 NormalZ=1 AngleXU=0 Radius=1.5 StartAngle=4.71239 EndAngle=7.85398
    g14: ArcOfCircle CenterX=-1.5 CenterY=56.25 CenterZ=0 NormalX=0 NormalY=0 NormalZ=1 AngleXU=0 Radius=1.5 StartAngle=4.71239 EndAngle=7.85398
    g15: ArcOfCircle CenterX=-11.49 CenterY=50.5 CenterZ=0 NormalX=0 NormalY=0 NormalZ=1 AngleXU=0 Radius=1.5 StartAngle=4.71239 EndAngle=7.85398
    g16: ArcOfCircle CenterX=-16.28 CenterY=44.75 CenterZ=0 NormalX=0 NormalY=0 NormalZ=1 AngleXU=0 Radius=1.5 StartAngle=4.71239 EndAngle=7.85398
    g17: ArcOfCircle CenterX=-18.2337 CenterY=39 CenterZ=0 NormalX=0 NormalY=0 NormalZ=1 AngleXU=0 Radius=1.5 StartAngle=4.71485 EndAngle=7.85398
    g18: ArcOfCircle CenterX=-16.2837 CenterY=27.25 CenterZ=0 NormalX=0 NormalY=0 NormalZ=1 AngleXU=0 Radius=1.5 StartAngle=4.71485 EndAngle=7.85398
    g19: ArcOfCircle CenterX=-18.2337 CenterY=33 CenterZ=0 NormalX=0 NormalY=0 NormalZ=1 AngleXU=0 Radius=1.5 StartAngle=4.71485 EndAngle=7.85398
    g20: ArcOfCircle CenterX=-11.49 CenterY=21.5 CenterZ=0 NormalX=0 NormalY=0 NormalZ=1 AngleXU=0 Radius=1.5 StartAngle=4.71239 EndAngle=7.85398
    g21: ArcOfCircle CenterX=-1.5 CenterY=4.25 CenterZ=0 NormalX=0 NormalY=0 NormalZ=1 AngleXU=0 Radius=1.5 StartAngle=4.71239 EndAngle=7.85398
    g22: ArcOfCircle CenterX=-1.5 CenterY=10 CenterZ=0 NormalX=0 NormalY=0 NormalZ=1 AngleXU=0 Radius=1.5 StartAngle=4.71239 EndAngle=7.85398
    g23: ArcOfCircle CenterX=-1.5 CenterY=15.75 CenterZ=0 NormalX=0 NormalY=0 NormalZ=1 AngleXU=0 Radius=1.5 StartAngle=4.71239 EndAngle=7.85398
    g24: LineSegment StartX=-49.19 StartY=69.25 StartZ=0 EndX=-1.5 EndY=69.25 EndZ=0
    g25: LineSegment StartX=-49.19 StartY=66.25 StartZ=0 EndX=-1.5 EndY=66.25 EndZ=0
    g26: LineSegment StartX=-49.19 StartY=63.5 StartZ=0 EndX=-1.5 EndY=63.5 EndZ=0
    g27: LineSegment StartX=-49.19 StartY=60.5 StartZ=0 EndX=-1.5 EndY=60.5 EndZ=0
    g28: LineSegment StartX=-49.19 StartY=57.75 StartZ=0 EndX=-1.5 EndY=57.75 EndZ=0
    g29: LineSegment StartX=-49.19 StartY=54.75 StartZ=0 EndX=-1.5 EndY=54.75 EndZ=0
    g30: LineSegment StartX=-49.19 StartY=52 StartZ=0 EndX=-11.49 EndY=52 EndZ=0
    g31: LineSegment StartX=-49.19 StartY=49 StartZ=0 EndX=-11.49 EndY=49 EndZ=0
    g32: LineSegment StartX=-49.19 StartY=46.25 StartZ=0 EndX=-16.28 EndY=46.25 EndZ=0
    g33: LineSegment StartX=-49.19 StartY=43.25 StartZ=0 EndX=-16.28 EndY=43.25 EndZ=0
    g34: LineSegment StartX=-49.19 StartY=40.5 StartZ=0 EndX=-18.2337 EndY=40.5 EndZ=0
    g35: LineSegment StartX=-49.19 StartY=37.5 StartZ=0 EndX=-18.23 EndY=37.5 EndZ=0
    g36: LineSegment StartX=-49.19 StartY=34.5 StartZ=0 EndX=-18.2337 EndY=34.5 EndZ=0
    g37: LineSegment StartX=-49.19 StartY=31.5 StartZ=0 EndX=-18.23 EndY=31.5 EndZ=0
    g38: LineSegment StartX=-49.19 StartY=28.75 StartZ=0 EndX=-16.2837 EndY=28.75 EndZ=0
    g39: LineSegment StartX=-49.19 StartY=25.75 StartZ=0 EndX=-16.28 EndY=25.75 EndZ=0
    g40: LineSegment StartX=-49.19 StartY=23 StartZ=0 EndX=-11.49 EndY=23 EndZ=0
    g41: LineSegment StartX=-49.19 StartY=20 StartZ=0 EndX=-11.49 EndY=20 EndZ=0
    g42: LineSegment StartX=-49.19 StartY=17.25 StartZ=0 EndX=-1.5 EndY=17.25 EndZ=0
    g43: LineSegment StartX=-49.19 StartY=14.25 StartZ=0 EndX=-1.5 EndY=14.25 EndZ=0
    g44: LineSegment StartX=-49.19 StartY=11.5 StartZ=0 EndX=-1.5 EndY=11.5 EndZ=0
    g45: LineSegment StartX=-49.19 StartY=8.5 StartZ=0 EndX=-1.5 EndY=8.5 EndZ=0
    g46: LineSegment StartX=-49.19 StartY=5.75 StartZ=0 EndX=-1.5 EndY=5.75 EndZ=0
    g47: LineSegment StartX=-49.19 StartY=2.75 StartZ=0 EndX=-1.5 EndY=2.75 EndZ=0
  constraints (120):
    c: Vertical(g0)
    c: Distance(g0) = 3
    c: Block(g0)
    c: Vertical(g1)
    c: Distance(g1) = 3
    c: Vertical(g2)
    c: Equal(g0,g2) = 3
    c: Block(g2)
    c: Vertical(g3)
    c: Equal(g1,g3) = 3
    c: Vertical(g4)
    c: Equal(g0,g4) = 3
    c: Block(g4)
    c: Vertical(g5)
    c: Equal(g1,g5) = 3
    c: Vertical(g6)
    c: Equal(g0,g6) = 3
    c: Block(g6)
    c: Vertical(g7)
    c: Equal(g1,g7) = 3
    c: Vertical(g8)
    c: Equal(g0,g8) = 3
    c: Block(g8)
    c: Vertical(g9)
    c: Equal(g1,g9) = 3
    c: Vertical(g10)
    c: Equal(g0,g10) = 3
    c: Block(g10)
    c: Vertical(g11)
    c: Equal(g1,g11) = 3
    c: Block(g12)
    c: Block(g13)
    c: Block(g14)
    c: Block(g15)
    c: Block(g16)
    c: Block(g17)
    c: Block(g18)
    c: Block(g19)
    c: Block(g20)
    c: Block(g21)
    c: Block(g22)
    c: Block(g23)
    c: Block(g11)
    c: Block(g9)
    c: Block(g7)
    c: Block(g5)
    c: Block(g3)
    c: Block(g1)
    c: Coincident(g24,g0)
    c: Coincident(g24,g12)
    c: Horizontal(g24)
    c: Coincident(g25,g0)
    c: Coincident(g25,g12)
    c: Horizontal(g25)
    c: Coincident(g26,g1)
    c: Coincident(g26,g13)
    c: Horizontal(g26)
    c: Coincident(g27,g1)
    c: Coincident(g27,g13)
    c: Horizontal(g27)
    c: Coincident(g28,g2)
    c: Coincident(g28,g14)
    c: Horizontal(g28)
    c: Coincident(g29,g2)
    c: Coincident(g29,g14)
    c: Horizontal(g29)
    c: Coincident(g30,g3)
    c: Coincident(g30,g15)
    c: Horizontal(g30)
    c: Coincident(g31,g3)
    c: Coincident(g31,g15)
    c: Horizontal(g31)
    c: Coincident(g32,g4)
    c: Coincident(g32,g16)
    c: Horizontal(g32)
    c: Coincident(g33,g4)
    c: Coincident(g33,g16)
    c: Horizontal(g33)
    c: Coincident(g34,g5)
    c: Coincident(g34,g17)
    c: Horizontal(g34)
    c: Coincident(g35,g5)
    c: Coincident(g35,g17)
    c: Horizontal(g35)
    c: Coincident(g36,g6)
    c: Coincident(g36,g19)
    c: Horizontal(g36)
    c: Coincident(g37,g6)
    c: Coincident(g37,g19)
    c: Horizontal(g37)
    c: Coincident(g38,g7)
    c: Coincident(g38,g18)
    c: Horizontal(g38)
    c: Coincident(g39,g7)
    c: Coincident(g39,g18)
    c: Horizontal(g39)
    c: Coincident(g40,g8)
    c: Coincident(g40,g20)
    c: Horizontal(g40)
    c: Coincident(g41,g8)
    c: Coincident(g41,g20)
    c: Horizontal(g41)
    c: Coincident(g42,g9)
    c: Coincident(g42,g23)
    c: Horizontal(g42)
    c: Coincident(g43,g9)
    c: Coincident(g43,g23)
    c: Horizontal(g43)
    c: Coincident(g44,g10)
    c: Coincident(g44,g22)
    c: Horizontal(g44)
    c: Coincident(g45,g10)
    c: Coincident(g45,g22)
    c: Horizontal(g45)
    c: Coincident(g46,g11)
    c: Coincident(g46,g21)
    c: Horizontal(g46)
    c: Coincident(g47,g11)
    c: Coincident(g47,g21)
    c: Horizontal(g47)
FEATURE [Sketcher::SketchObject] Sketch031
  FullyConstrained = true
  Placement = pos=(117,19,0) rot=(0.57735,0.57735,0.57735;2.0944rad)
  sketch-geometry (24):
    g0: ArcOfCircle CenterX=-49.19 CenterY=67.75 CenterZ=0 NormalX=0 NormalY=0 NormalZ=1 AngleXU=0 Radius=1.5 StartAngle=1.5708 EndAngle=4.71239
    g1: ArcOfCircle CenterX=-49.19 CenterY=62 CenterZ=0 NormalX=0 NormalY=0 NormalZ=1 AngleXU=0 Radius=1.5 StartAngle=1.5708 EndAngle=4.71239
    g2: ArcOfCircle CenterX=-49.19 CenterY=56.25 CenterZ=0 NormalX=0 NormalY=0 NormalZ=1 AngleXU=0 Radius=1.5 StartAngle=1.5708 EndAngle=4.71239
    g3: ArcOfCircle CenterX=-49.19 CenterY=50.5 CenterZ=0 NormalX=0 NormalY=0 NormalZ=1 AngleXU=0 Radius=1.5 StartAngle=1.5708 EndAngle=4.71239
    g4: ArcOfCircle CenterX=-49.19 CenterY=44.75 CenterZ=0 NormalX=0 NormalY=0 NormalZ=1 AngleXU=0 Radius=1.5 StartAngle=1.5708 EndAngle=4.71239
    g5: ArcOfCircle CenterX=-49.19 CenterY=39 CenterZ=0 NormalX=0 NormalY=0 NormalZ=1 AngleXU=0 Radius=1.5 StartAngle=1.5708 EndAngle=4.71239
    g6: ArcOfCircle CenterX=-49.19 CenterY=33 CenterZ=0 NormalX=0 NormalY=0 NormalZ=1 AngleXU=0 Radius=1.5 StartAngle=1.5708 EndAngle=4.71239
    g7: ArcOfCircle CenterX=-49.19 CenterY=27.25 CenterZ=0 NormalX=0 NormalY=0 NormalZ=1 AngleXU=0 Radius=1.5 StartAngle=1.5708 EndAngle=4.71239
    g8: ArcOfCircle CenterX=-49.19 CenterY=21.5 CenterZ=0 NormalX=0 NormalY=0 NormalZ=1 AngleXU=0 Radius=1.5 StartAngle=1.5708 EndAngle=4.71239
    g9: ArcOfCircle CenterX=-49.19 CenterY=15.75 CenterZ=0 NormalX=0 NormalY=0 NormalZ=1 AngleXU=0 Radius=1.5 StartAngle=1.5708 EndAngle=4.71239
    g10: ArcOfCircle CenterX=-49.19 CenterY=10 CenterZ=0 NormalX=0 NormalY=0 NormalZ=1 AngleXU=0 Radius=1.5 StartAngle=1.5708 EndAngle=4.71239
    g11: ArcOfCircle CenterX=-49.19 CenterY=4.25 CenterZ=0 NormalX=0 NormalY=0 NormalZ=1 AngleXU=0 Radius=1.5 StartAngle=1.5708 EndAngle=4.71239
    g12: LineSegment StartX=-49.19 StartY=69.25 StartZ=0 EndX=-49.19 EndY=66.25 EndZ=0
    g13: LineSegment StartX=-49.19 StartY=63.5 StartZ=0 EndX=-49.19 EndY=60.5 EndZ=0
    g14: LineSegment StartX=-49.19 StartY=57.75 StartZ=0 EndX=-49.19 EndY=54.75 EndZ=0
    g15: LineSegment StartX=-49.19 StartY=52 StartZ=0 EndX=-49.19 EndY=49 EndZ=0
    g16: LineSegment StartX=-49.19 StartY=46.25 StartZ=0 EndX=-49.19 EndY=43.25 EndZ=0
    g17: LineSegment StartX=-49.19 StartY=40.5 StartZ=0 EndX=-49.19 EndY=37.5 EndZ=0
    g18: LineSegment StartX=-49.19 StartY=34.5 StartZ=0 EndX=-49.19 EndY=31.5 EndZ=0
    g19: LineSegment StartX=-49.19 StartY=28.75 StartZ=0 EndX=-49.19 EndY=25.75 EndZ=0
    g20: LineSegment StartX=-49.19 StartY=23 StartZ=0 EndX=-49.19 EndY=20 EndZ=0
    g21: LineSegment StartX=-49.19 StartY=17.25 StartZ=0 EndX=-49.19 EndY=14.25 EndZ=0
    g22: LineSegment StartX=-49.19 StartY=11.5 StartZ=0 EndX=-49.19 EndY=8.5 EndZ=0
    g23: LineSegment StartX=-49.19 StartY=5.75 StartZ=0 EndX=-49.19 EndY=2.75 EndZ=0
  constraints (48):
    c: Block(g0)
    c: Block(g1)
    c: Block(g2)
    c: Block(g3)
    c: Block(g4)
    c: Block(g5)
    c: Block(g6)
    c: Block(g7)
    c: Block(g8)
    c: Block(g9)
    c: Block(g10)
    c: Block(g11)
    c: Coincident(g12,g0)
    c: Coincident(g12,g0)
    c: Vertical(g12)
    c: Vertical(g13)
    c: Coincident(g13,g1)
    c: Vertical(g14)
    c: Coincident(g14,g2)
    c: Vertical(g15)
    c: Coincident(g15,g3)
    c: Vertical(g16)
    c: Coincident(g16,g4)
    c: Vertical(g17)
    c: Coincident(g17,g5)
    c: Vertical(g18)
    c: Coincident(g18,g6)
    c: Vertical(g19)
    c: Coincident(g19,g7)
    c: Vertical(g20)
    c: Coincident(g20,g8)
    c: Vertical(g21)
    c: Coincident(g21,g9)
    c: Vertical(g22)
    c: Coincident(g22,g10)
    c: Vertical(g23)
    c: Coincident(g23,g11)
    c: Block(g23)
    c: Block(g22)
    c: Block(g21)
    c: Block(g20)
    c: Block(g13)
    c: Block(g14)
    c: Block(g15)
    c: Block(g16)
    c: Block(g17)
    c: Block(g18)
    c: Block(g19)
FEATURE [Part::Extrusion] Extrude022
  Base = -> Sketch030
  Dir = (1,-2e-16,2e-16)
  DirMode = 2
  FaceMakerClass = Part::FaceMakerBullseye
  LengthFwd = 19
  LengthRev = 0
  Placement = pos=(-19,0,0) rot=(0,0,1;0rad)
  Solid = true
  Symmetric = false
FEATURE [Part::Fillet] Fillet022
  Base = -> Extrude022
  Edges = 24 edges r=1.49: [Edge6,Edge11,Edge18,Edge23,Edge30,Edge35,Edge42,Edge47,Edge54,Edge59,Edge66,Edge71,Edge78,Edge83,Edge90,Edge95,Edge102,Edge107,Edge114,Edge119,Edge126,Edge131,Edge138,Edge143]
FEATURE [Part::Cut] Cut020  label="top010"
  Base = -> Cut019
  Tool = -> Fillet022
FEATURE [Sketcher::SketchObject] Sketch032
  FullyConstrained = true
  Placement = pos=(117,19,0) rot=(0.57735,0.57735,0.57735;2.0944rad)
  sketch-geometry (48):
    g0: LineSegment StartX=-49.19 StartY=69.25 StartZ=0 EndX=-49.19 EndY=66.25 EndZ=0
    g1: LineSegment StartX=-49.19 StartY=63.5 StartZ=0 EndX=-49.19 EndY=60.5 EndZ=0
    g2: LineSegment StartX=-49.19 StartY=57.75 StartZ=0 EndX=-49.19 EndY=54.75 EndZ=0
    g3: LineSegment StartX=-49.19 StartY=52 StartZ=0 EndX=-49.19 EndY=49 EndZ=0
    g4: LineSegment StartX=-49.19 StartY=46.25 StartZ=0 EndX=-49.19 EndY=43.25 EndZ=0
    g5: LineSegment StartX=-49.19 StartY=40.5 StartZ=0 EndX=-49.19 EndY=37.5 EndZ=0
    g6: LineSegment StartX=-49.19 StartY=34.5 StartZ=0 EndX=-49.19 EndY=31.5 EndZ=0
    g7: LineSegment StartX=-49.19 StartY=28.75 StartZ=0 EndX=-49.19 EndY=25.75 EndZ=0
    g8: LineSegment StartX=-49.19 StartY=23 StartZ=0 EndX=-49.19 EndY=20 EndZ=0
    g9: LineSegment StartX=-49.19 StartY=17.25 StartZ=0 EndX=-49.19 EndY=14.25 EndZ=0
    g10: LineSegment StartX=-49.19 StartY=11.5 StartZ=0 EndX=-49.19 EndY=8.5 EndZ=0
    g11: LineSegment StartX=-49.19 StartY=5.75 StartZ=0 EndX=-49.19 EndY=2.75 EndZ=0
    g12: ArcOfCircle CenterX=-1.5 CenterY=67.75 CenterZ=0 NormalX=0 NormalY=0 NormalZ=1 AngleXU=0 Radius=1.5 StartAngle=4.71239 EndAngle=7.85398
    g13: ArcOfCircle CenterX=-1.5 CenterY=62 CenterZ=0 NormalX=0 NormalY=0 NormalZ=1 AngleXU=0 Radius=1.5 StartAngle=4.71239 EndAngle=7.85398
    g14: ArcOfCircle CenterX=-1.5 CenterY=56.25 CenterZ=0 NormalX=0 NormalY=0 NormalZ=1 AngleXU=0 Radius=1.5 StartAngle=4.71239 EndAngle=7.85398
    g15: ArcOfCircle CenterX=-11.49 CenterY=50.5 CenterZ=0 NormalX=0 NormalY=0 NormalZ=1 AngleXU=0 Radius=1.5 StartAngle=4.71239 EndAngle=7.85398
    g16: ArcOfCircle CenterX=-16.28 CenterY=44.75 CenterZ=0 NormalX=0 NormalY=0 NormalZ=1 AngleXU=0 Radius=1.5 StartAngle=4.71239 EndAngle=7.85398
    g17: ArcOfCircle CenterX=-18.2337 CenterY=39 CenterZ=0 NormalX=0 NormalY=0 NormalZ=1 AngleXU=0 Radius=1.5 StartAngle=4.71485 EndAngle=7.85398
    g18: ArcOfCircle CenterX=-16.2837 CenterY=27.25 CenterZ=0 NormalX=0 NormalY=0 NormalZ=1 AngleXU=0 Radius=1.5 StartAngle=4.71485 EndAngle=7.85398
    g19: ArcOfCircle CenterX=-18.2337 CenterY=33 CenterZ=0 NormalX=0 NormalY=0 NormalZ=1 AngleXU=0 Radius=1.5 StartAngle=4.71485 EndAngle=7.85398
    g20: ArcOfCircle CenterX=-11.49 CenterY=21.5 CenterZ=0 NormalX=0 NormalY=0 NormalZ=1 AngleXU=0 Radius=1.5 StartAngle=4.71239 EndAngle=7.85398
    g21: ArcOfCircle CenterX=-1.5 CenterY=4.25 CenterZ=0 NormalX=0 NormalY=0 NormalZ=1 AngleXU=0 Radius=1.5 StartAngle=4.71239 EndAngle=7.85398
    g22: ArcOfCircle CenterX=-1.5 CenterY=10 CenterZ=0 NormalX=0 NormalY=0 NormalZ=1 AngleXU=0 Radius=1.5 StartAngle=4.71239 EndAngle=7.85398
    g23: ArcOfCircle CenterX=-1.5 CenterY=15.75 CenterZ=0 NormalX=0 NormalY=0 NormalZ=1 AngleXU=0 Radius=1.5 StartAngle=4.71239 EndAngle=7.85398
    g24: LineSegment StartX=-49.19 StartY=69.25 StartZ=0 EndX=-1.5 EndY=69.25 EndZ=0
    g25: LineSegment StartX=-49.19 StartY=66.25 StartZ=0 EndX=-1.5 EndY=66.25 EndZ=0
    g26: LineSegment StartX=-49.19 StartY=63.5 StartZ=0 EndX=-1.5 EndY=63.5 EndZ=0
    g27: LineSegment StartX=-49.19 StartY=60.5 StartZ=0 EndX=-1.5 EndY=60.5 EndZ=0
    g28: LineSegment StartX=-49.19 StartY=57.75 StartZ=0 EndX=-1.5 EndY=57.75 EndZ=0
    g29: LineSegment StartX=-49.19 StartY=54.75 StartZ=0 EndX=-1.5 EndY=54.75 EndZ=0
    g30: LineSegment StartX=-49.19 StartY=52 StartZ=0 EndX=-11.49 EndY=52 EndZ=0
    g31: LineSegment StartX=-49.19 StartY=49 StartZ=0 EndX=-11.49 EndY=49 EndZ=0
    g32: LineSegment StartX=-49.19 StartY=46.25 StartZ=0 EndX=-16.28 EndY=46.25 EndZ=0
    g33: LineSegment StartX=-49.19 StartY=43.25 StartZ=0 EndX=-16.28 EndY=43.25 EndZ=0
    g34: LineSegment StartX=-49.19 StartY=40.5 StartZ=0 EndX=-18.2337 EndY=40.5 EndZ=0
    g35: LineSegment StartX=-49.19 StartY=37.5 StartZ=0 EndX=-18.23 EndY=37.5 EndZ=0
    g36: LineSegment StartX=-49.19 StartY=34.5 StartZ=0 EndX=-18.2337 EndY=34.5 EndZ=0
    g37: LineSegment StartX=-49.19 StartY=31.5 StartZ=0 EndX=-18.23 EndY=31.5 EndZ=0
    g38: LineSegment StartX=-49.19 StartY=28.75 StartZ=0 EndX=-16.2837 EndY=28.75 EndZ=0
    g39: LineSegment StartX=-49.19 StartY=25.75 StartZ=0 EndX=-16.28 EndY=25.75 EndZ=0
    g40: LineSegment StartX=-49.19 StartY=23 StartZ=0 EndX=-11.49 EndY=23 EndZ=0
    g41: LineSegment StartX=-49.19 StartY=20 StartZ=0 EndX=-11.49 EndY=20 EndZ=0
    g42: LineSegment StartX=-49.19 StartY=17.25 StartZ=0 EndX=-1.5 EndY=17.25 EndZ=0
    g43: LineSegment StartX=-49.19 StartY=14.25 StartZ=0 EndX=-1.5 EndY=14.25 EndZ=0
    g44: LineSegment StartX=-49.19 StartY=11.5 StartZ=0 EndX=-1.5 EndY=11.5 EndZ=0
    g45: LineSegment StartX=-49.19 StartY=8.5 StartZ=0 EndX=-1.5 EndY=8.5 EndZ=0
    g46: LineSegment StartX=-49.19 StartY=5.75 StartZ=0 EndX=-1.5 EndY=5.75 EndZ=0
    g47: LineSegment StartX=-49.19 StartY=2.75 StartZ=0 EndX=-1.5 EndY=2.75 EndZ=0
  constraints (120):
    c: Vertical(g0)
    c: Distance(g0) = 3
    c: Block(g0)
    c: Vertical(g1)
    c: Distance(g1) = 3
    c: Vertical(g2)
    c: Equal(g0,g2) = 3
    c: Block(g2)
    c: Vertical(g3)
    c: Equal(g1,g3) = 3
    c: Vertical(g4)
    c: Equal(g0,g4) = 3
    c: Block(g4)
    c: Vertical(g5)
    c: Equal(g1,g5) = 3
    c: Vertical(g6)
    c: Equal(g0,g6) = 3
    c: Block(g6)
    c: Vertical(g7)
    c: Equal(g1,g7) = 3
    c: Vertical(g8)
    c: Equal(g0,g8) = 3
    c: Block(g8)
    c: Vertical(g9)
    c: Equal(g1,g9) = 3
    c: Vertical(g10)
    c: Equal(g0,g10) = 3
    c: Block(g10)
    c: Vertical(g11)
    c: Equal(g1,g11) = 3
    c: Block(g12)
    c: Block(g13)
    c: Block(g14)
    c: Block(g15)
    c: Block(g16)
    c: Block(g17)
    c: Block(g18)
    c: Block(g19)
    c: Block(g20)
    c: Block(g21)
    c: Block(g22)
    c: Block(g23)
    c: Block(g11)
    c: Block(g9)
    c: Block(g7)
    c: Block(g5)
    c: Block(g3)
    c: Block(g1)
    c: Coincident(g24,g0)
    c: Coincident(g24,g12)
    c: Horizontal(g24)
    c: Coincident(g25,g0)
    c: Coincident(g25,g12)
    c: Horizontal(g25)
    c: Coincident(g26,g1)
    c: Coincident(g26,g13)
    c: Horizontal(g26)
    c: Coincident(g27,g1)
    c: Coincident(g27,g13)
    c: Horizontal(g27)
    c: Coincident(g28,g2)
    c: Coincident(g28,g14)
    c: Horizontal(g28)
    c: Coincident(g29,g2)
    c: Coincident(g29,g14)
    c: Horizontal(g29)
    c: Coincident(g30,g3)
    c: Coincident(g30,g15)
    c: Horizontal(g30)
    c: Coincident(g31,g3)
    c: Coincident(g31,g15)
    c: Horizontal(g31)
    c: Coincident(g32,g4)
    c: Coincident(g32,g16)
    c: Horizontal(g32)
    c: Coincident(g33,g4)
    c: Coincident(g33,g16)
    c: Horizontal(g33)
    c: Coincident(g34,g5)
    c: Coincident(g34,g17)
    c: Horizontal(g34)
    c: Coincident(g35,g5)
    c: Coincident(g35,g17)
    c: Horizontal(g35)
    c: Coincident(g36,g6)
    c: Coincident(g36,g19)
    c: Horizontal(g36)
    c: Coincident(g37,g6)
    c: Coincident(g37,g19)
    c: Horizontal(g37)
    c: Coincident(g38,g7)
    c: Coincident(g38,g18)
    c: Horizontal(g38)
    c: Coincident(g39,g7)
    c: Coincident(g39,g18)
    c: Horizontal(g39)
    c: Coincident(g40,g8)
    c: Coincident(g40,g20)
    c: Horizontal(g40)
    c: Coincident(g41,g8)
    c: Coincident(g41,g20)
    c: Horizontal(g41)
    c: Coincident(g42,g9)
    c: Coincident(g42,g23)
    c: Horizontal(g42)
    c: Coincident(g43,g9)
    c: Coincident(g43,g23)
    c: Horizontal(g43)
    c: Coincident(g44,g10)
    c: Coincident(g44,g22)
    c: Horizontal(g44)
    c: Coincident(g45,g10)
    c: Coincident(g45,g22)
    c: Horizontal(g45)
    c: Coincident(g46,g11)
    c: Coincident(g46,g21)
    c: Horizontal(g46)
    c: Coincident(g47,g11)
    c: Coincident(g47,g21)
    c: Horizontal(g47)
FEATURE [Part::Extrusion] Extrude023
  Base = -> Sketch032
  Dir = (1,-2e-16,2e-16)
  DirMode = 2
  FaceMakerClass = Part::FaceMakerBullseye
  LengthFwd = 19
  LengthRev = 0
  Placement = pos=(-19,0,0) rot=(0,0,1;0rad)
  Solid = true
  Symmetric = false
FEATURE [Part::Fillet] Fillet023
  Base = -> Extrude023
  Edges = 24 edges r=1.49: [Edge6,Edge11,Edge18,Edge23,Edge30,Edge35,Edge42,Edge47,Edge54,Edge59,Edge66,Edge71,Edge78,Edge83,Edge90,Edge95,Edge102,Edge107,Edge114,Edge119,Edge126,Edge131,Edge138,Edge143]
  Placement = pos=(0,0.05,0) rot=(0,0,1;0rad)
FEATURE [Part::Cut] Cut014  label="bottom003"
  Base = -> Cut007
  Tool = -> Fusion047
FEATURE [Part::Cut] Cut021  label="bottom004"
  Base = -> Cut014
  Tool = -> Fillet023
FEATURE [Sketcher::SketchObject] Sketch033
  FullyConstrained = true
  Placement = pos=(117,19,0) rot=(0.57735,0.57735,0.57735;2.0944rad)
  sketch-geometry (8):
    g0: LineSegment StartX=-49.19 StartY=69.25 StartZ=0 EndX=-49.19 EndY=66.25 EndZ=0
    g1: LineSegment StartX=-49.19 StartY=5.75 StartZ=0 EndX=-49.19 EndY=2.75 EndZ=0
    g2: ArcOfCircle CenterX=-1.5 CenterY=67.75 CenterZ=0 NormalX=0 NormalY=0 NormalZ=1 AngleXU=0 Radius=1.5 StartAngle=4.71239 EndAngle=7.85398
    g3: ArcOfCircle CenterX=-1.5 CenterY=4.25 CenterZ=0 NormalX=0 NormalY=0 NormalZ=1 AngleXU=0 Radius=1.5 StartAngle=4.71239 EndAngle=7.85398
    g4: LineSegment StartX=-49.19 StartY=69.25 StartZ=0 EndX=-1.5 EndY=69.25 EndZ=0
    g5: LineSegment StartX=-49.19 StartY=66.25 StartZ=0 EndX=-1.5 EndY=66.25 EndZ=0
    g6: LineSegment StartX=-49.19 StartY=5.75 StartZ=0 EndX=-1.5 EndY=5.75 EndZ=0
    g7: LineSegment StartX=-49.19 StartY=2.75 StartZ=0 EndX=-1.5 EndY=2.75 EndZ=0
  constraints (19):
    c: Vertical(g0)
    c: Distance(g0) = 3
    c: Block(g0)
    c: Vertical(g1)
    c: Block(g2)
    c: Block(g3)
    c: Block(g1)
    c: Coincident(g4,g0)
    c: Coincident(g4,g2)
    c: Horizontal(g4)
    c: Coincident(g5,g0)
    c: Coincident(g5,g2)
    c: Horizontal(g5)
    c: Coincident(g6,g1)
    c: Coincident(g6,g3)
    c: Horizontal(g6)
    c: Coincident(g7,g1)
    c: Coincident(g7,g3)
    c: Horizontal(g7)
FEATURE [Sketcher::SketchObject] Sketch034
  FullyConstrained = true
  Placement = pos=(117,19,0) rot=(0.57735,0.57735,0.57735;2.0944rad)
  sketch-geometry (8):
    g0: LineSegment StartX=-49.19 StartY=63.5 StartZ=0 EndX=-49.19 EndY=60.5 EndZ=0
    g1: LineSegment StartX=-49.19 StartY=11.5 StartZ=0 EndX=-49.19 EndY=8.5 EndZ=0
    g2: ArcOfCircle CenterX=-1.5 CenterY=62 CenterZ=0 NormalX=0 NormalY=0 NormalZ=1 AngleXU=0 Radius=1.5 StartAngle=4.71239 EndAngle=7.85398
    g3: ArcOfCircle CenterX=-1.5 CenterY=10 CenterZ=0 NormalX=0 NormalY=0 NormalZ=1 AngleXU=0 Radius=1.5 StartAngle=4.71239 EndAngle=7.85398
    g4: LineSegment StartX=-49.19 StartY=63.5 StartZ=0 EndX=-1.5 EndY=63.5 EndZ=0
    g5: LineSegment StartX=-49.19 StartY=60.5 StartZ=0 EndX=-1.5 EndY=60.5 EndZ=0
    g6: LineSegment StartX=-49.19 StartY=11.5 StartZ=0 EndX=-1.5 EndY=11.5 EndZ=0
    g7: LineSegment StartX=-49.19 StartY=8.5 StartZ=0 EndX=-1.5 EndY=8.5 EndZ=0
  constraints (19):
    c: Vertical(g0)
    c: Distance(g0) = 3
    c: Vertical(g1)
    c: Block(g1)
    c: Block(g2)
    c: Block(g3)
    c: Block(g0)
    c: Coincident(g4,g0)
    c: Coincident(g4,g2)
    c: Horizontal(g4)
    c: Coincident(g5,g0)
    c: Coincident(g5,g2)
    c: Horizontal(g5)
    c: Coincident(g6,g1)
    c: Coincident(g6,g3)
    c: Horizontal(g6)
    c: Coincident(g7,g1)
    c: Coincident(g7,g3)
    c: Horizontal(g7)
FEATURE [Part::Extrusion] Extrude024
  Base = -> Sketch033
  Dir = (1,0,0)
  DirMode = 2
  FaceMakerClass = Part::FaceMakerBullseye
  LengthFwd = 10
  LengthRev = 0
  Solid = true
  Symmetric = false
FEATURE [Part::Extrusion] Extrude025
  Base = -> Sketch034
  Dir = (1,0,0)
  DirMode = 2
  FaceMakerClass = Part::FaceMakerBullseye
  LengthFwd = 10
  LengthRev = 0
  Solid = true
  Symmetric = false
FEATURE [Part::Fillet] Fillet024  label="removeFromtMoreFrontCaseScrewRetainers"
  Base = -> Extrude024
  Edges = 4 edges r=1.49: [Edge6,Edge11,Edge18,Edge23]
  Placement = pos=(-11,0,0) rot=(0,0,1;0rad)
FEATURE [Part::Fillet] Fillet025  label="removeFromtMoreFrontCaseScrewRetainers001"
  Base = -> Extrude025
  Edges = 4 edges r=1.49: [Edge6,Edge11,Edge18,Edge23]
  Placement = pos=(-19,0,0) rot=(0,0,1;0rad)
FEATURE [Part::Cut] Cut022
  Base = -> Cut015
  Tool = -> Fillet025
FEATURE [Part::Cut] Cut023  label="screwRetainers"
  Base = -> Cut022
  Tool = -> Fillet024
FEATURE [Part::MultiFuse] Fusion056  label="bottom005"
  Shapes = -> [Fusion044,Cut021]
FEATURE [Part::MultiFuse] Fusion057  label="casePillars001"
  Shapes = -> [Cut016,Fusion052]
FEATURE [Part::MultiFuse] Fusion058  label="bottom006"
  Shapes = -> [Fusion056,Cut023]
FEATURE [Part::MultiFuse] Fusion059  label="bottom007"
  Shapes = -> [Fusion058,Fillet005]
FEATURE [Part::MultiFuse] Fusion060  label="bottom008"
  Shapes = -> [Fusion059,Fusion]
FEATURE [Part::MultiFuse] Fusion061  label="top011"
  Shapes = -> [Cut006,Cut020]
FEATURE [Part::MultiFuse] Fusion062  label="top012"
  Shapes = -> [Fusion057,Fusion061]
FEATURE [Part::MultiFuse] Fusion063  label="top013"
  Shapes = -> [Fusion062,Extrude003,Extrude002]
